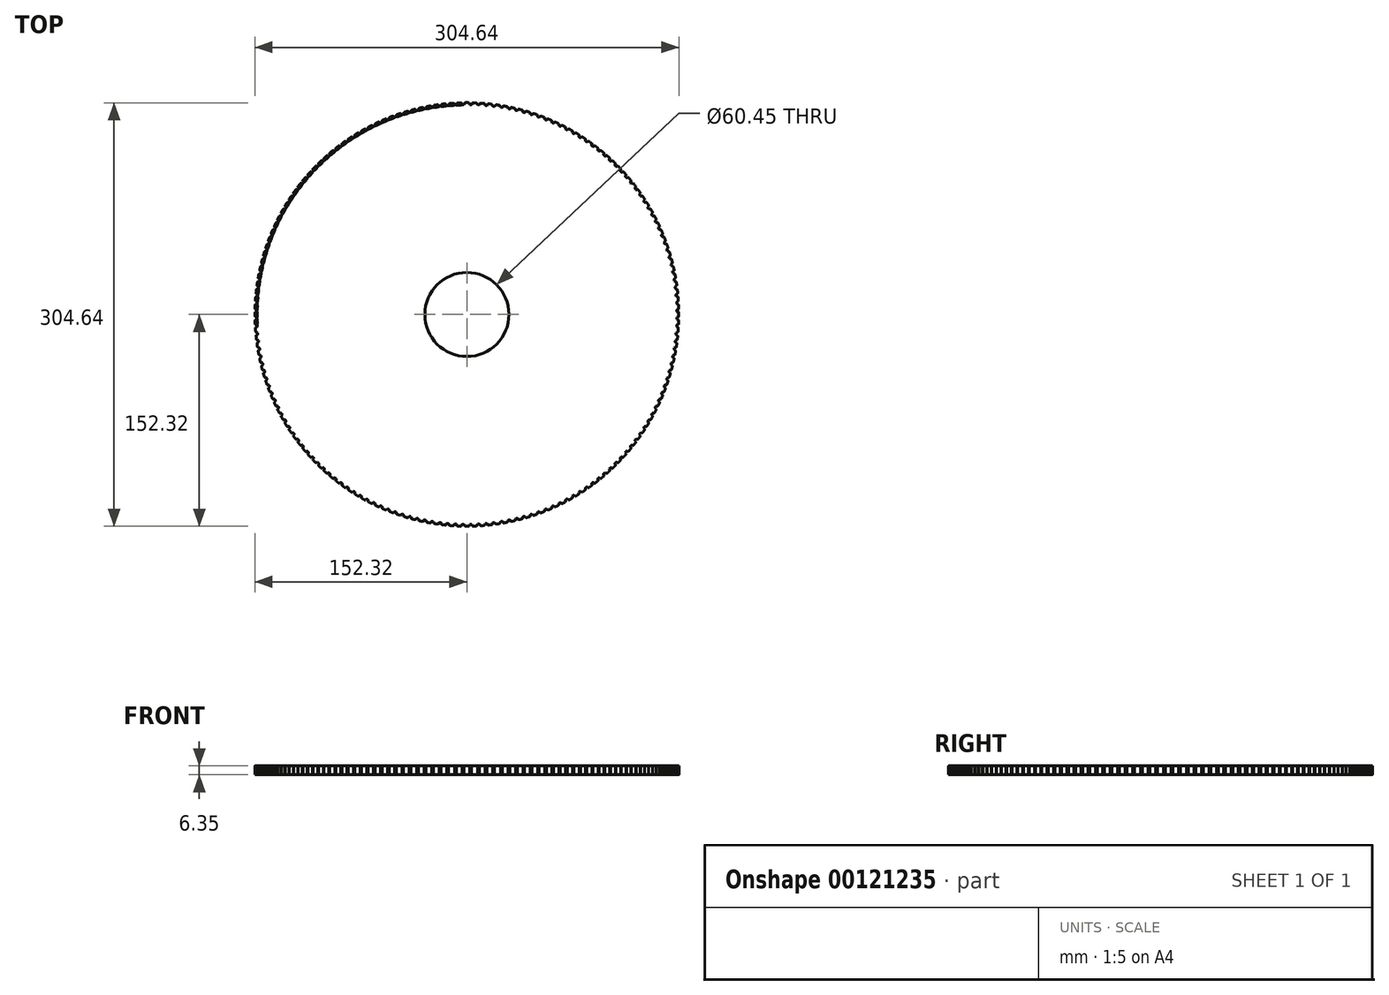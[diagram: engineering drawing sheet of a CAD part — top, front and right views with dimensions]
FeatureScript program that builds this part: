
annotation { "Feature Type Name" : "Feature", "Feature Type Description" : "" }
export const myFeature = defineFeature(function(context is Context, id is Id, definition is map)
    precondition{}
    {
        {
            var Q0;
            Q0=qCreatedBy(makeId("Top.planeOp"),FACE);
            var sketch = newSketch(context, id + "F0", { "sketchPlane" : qUnion([Q0])});
            skCircle(sketch, "E0", {"center": v(0, 0) * mm, "radius": 151 * mm});
            skSolve(sketch);
        }
        {
            var Q0;
            Q0=qSketchRegion(id+"F0",true);
            extrude(context, id + "F1", {"entities" : qUnion([Q0]), "depth" : 6.35 * mm});
        }
        {
            var Q0;
            Q0=qCreatedBy(makeId("Top.planeOp"),FACE);
            var sketch = newSketch(context, id + "F2", { "sketchPlane" : qUnion([Q0])});
            skLineSegment(sketch, "E1", {"start": v(0, -0.08) * mm, "end": v(0, 183.08) * mm, "construction": true});
            skArc(sketch, "E2", {"start": v(1.26, 152.32) * mm, "mid": v(0, 152.32) * mm, "end": v(-1.26, 152.32) * mm});
            skLineSegment(sketch, "E3", {"start": v(-1.6, 152.1) * mm, "end": v(-2.1, 151.02) * mm});
            skLineSegment(sketch, "E4", {"start": v(1.6, 152.1) * mm, "end": v(2.1, 151.02) * mm});
            skPoint(sketch, "E5.visualSharp", {"position": v(-1.5, 152.32) * mm});
            skArc(sketch, "E5.filletArc", {"start": v(-1.26, 152.32) * mm, "mid": v(-1.46, 152.26) * mm, "end": v(-1.6, 152.1) * mm});
            skPoint(sketch, "E6.visualSharp", {"position": v(1.5, 152.32) * mm});
            skArc(sketch, "E6.filletArc", {"start": v(1.6, 152.1) * mm, "mid": v(1.46, 152.26) * mm, "end": v(1.26, 152.32) * mm});
            skArc(sketch, "E7", {"start": v(-2.27, 150.9) * mm, "mid": v(-2.17, 150.94) * mm, "end": v(-2.1, 151.02) * mm});
            skArc(sketch, "E8", {"start": v(2.1, 151.02) * mm, "mid": v(2.17, 150.94) * mm, "end": v(2.27, 150.9) * mm});
            skPoint(sketch, "E9.orphan", {"position": v(2.15, 150.91) * mm});
            skArc(sketch, "E10", {"start": v(-2.27, 150.9) * mm, "mid": v(0, 150.67) * mm, "end": v(2.27, 150.9) * mm});
            skSolve(sketch);
        }
        {
            var Q0;
            Q0=makeQuery(id+"F2.imprint","IMPRINT",FACE,{"disambiguationData":[TD([[makeQuery(id+"F2.imprint","IMPRINT",EDGE,{"derivedFrom":sQuery(id+"F2.wireOp",EDGE,"E2")}),1.0]])]});
            var Q1;
            Q1=makeQuery(id+"F2.imprint","IMPRINT",FACE,{"disambiguationData":[TD([[makeQuery(id+"F2.imprint","IMPRINT",EDGE,{"derivedFrom":sQuery(id+"F2.wireOp",EDGE,"bbfa1fc5-6552-4957-9194-8f10230bb92c.0")}),1.0]])]});
            var Q2;
            Q2=makeQuery(id+"F1.opExtrude","CAP_FACE",FACE,{"disambiguationData":[OSD([sQuery(id+"F0.wireOp",EDGE,"E0")])],"isStart":false});
            extrude(context, id + "F3", {"entities" : qUnion([Q0, Q1]), "endBound" : BoundingType.UP_TO_SURFACE, "endBoundEntityFace" : qUnion([Q2]), "depth" : 25.4 * mm});
        }
        {
            var Q0;
            Q0=qCreatedBy(makeId("Front.planeOp"),FACE);
            var sketch = newSketch(context, id + "F4", { "sketchPlane" : qUnion([Q0])});
            skLineSegment(sketch, "E11", {"start": v(0, 74.48) * mm, "end": v(0, -67.78) * mm, "construction": true});
            skSolve(sketch);
        }
        {
            var Q0;
            Q0=makeQuery(id+"F3.opExtrude","SWEPT_BODY",BODY,{"disambiguationData":[OSD([sQuery(id+"F2.wireOp",EDGE,"E2"),sQuery(id+"F2.wireOp",EDGE,"E3"),sQuery(id+"F2.wireOp",EDGE,"E4"),sQuery(id+"F2.wireOp",EDGE,"E5.filletArc"),sQuery(id+"F2.wireOp",EDGE,"E6.filletArc"),sQuery(id+"F2.wireOp",EDGE,"E7"),sQuery(id+"F2.wireOp",EDGE,"E8"),sQuery(id+"F2.wireOp",EDGE,"E10")])]});
            var Q1;
            Q1=sQuery(id+"F4.wireOp",EDGE,"E11");
            circularPattern(context, id + "F5", {"entities" : qUnion([Q0]), "axis" : qUnion([Q1]), "angle" : 360 * degree, "instanceCount" : 172, "equalSpace" : true});
        }
        {
            var Q0;
            Q0=makeQuery(id+"F1.opExtrude","SWEPT_BODY",BODY,{"disambiguationData":[OSD([sQuery(id+"F0.wireOp",EDGE,"E0")])]});
            var Q1;
            Q1=makeQuery(id+"F3.opExtrude","SWEPT_BODY",BODY,{"disambiguationData":[OSD([sQuery(id+"F2.wireOp",EDGE,"E2"),sQuery(id+"F2.wireOp",EDGE,"E3"),sQuery(id+"F2.wireOp",EDGE,"E4"),sQuery(id+"F2.wireOp",EDGE,"E5.filletArc"),sQuery(id+"F2.wireOp",EDGE,"E6.filletArc"),sQuery(id+"F2.wireOp",EDGE,"E7"),sQuery(id+"F2.wireOp",EDGE,"E8"),sQuery(id+"F2.wireOp",EDGE,"E10")])]});
            var Q2;
            Q2=makeQuery(id+"F5.opPattern","COPY",BODY,{"derivedFrom":makeQuery(id+"F3.opExtrude","SWEPT_BODY",BODY,{"disambiguationData":[OSD([sQuery(id+"F2.wireOp",EDGE,"E2"),sQuery(id+"F2.wireOp",EDGE,"E3"),sQuery(id+"F2.wireOp",EDGE,"E4"),sQuery(id+"F2.wireOp",EDGE,"E5.filletArc"),sQuery(id+"F2.wireOp",EDGE,"E6.filletArc"),sQuery(id+"F2.wireOp",EDGE,"E7"),sQuery(id+"F2.wireOp",EDGE,"E8"),sQuery(id+"F2.wireOp",EDGE,"E10")])]}),"instanceName":"1"});
            var Q3;
            Q3=makeQuery(id+"F5.opPattern","COPY",BODY,{"derivedFrom":makeQuery(id+"F3.opExtrude","SWEPT_BODY",BODY,{"disambiguationData":[OSD([sQuery(id+"F2.wireOp",EDGE,"E2"),sQuery(id+"F2.wireOp",EDGE,"E3"),sQuery(id+"F2.wireOp",EDGE,"E4"),sQuery(id+"F2.wireOp",EDGE,"E5.filletArc"),sQuery(id+"F2.wireOp",EDGE,"E6.filletArc"),sQuery(id+"F2.wireOp",EDGE,"E7"),sQuery(id+"F2.wireOp",EDGE,"E8"),sQuery(id+"F2.wireOp",EDGE,"E10")])]}),"instanceName":"2"});
            var Q4;
            Q4=makeQuery(id+"F5.opPattern","COPY",BODY,{"derivedFrom":makeQuery(id+"F3.opExtrude","SWEPT_BODY",BODY,{"disambiguationData":[OSD([sQuery(id+"F2.wireOp",EDGE,"E2"),sQuery(id+"F2.wireOp",EDGE,"E3"),sQuery(id+"F2.wireOp",EDGE,"E4"),sQuery(id+"F2.wireOp",EDGE,"E5.filletArc"),sQuery(id+"F2.wireOp",EDGE,"E6.filletArc"),sQuery(id+"F2.wireOp",EDGE,"E7"),sQuery(id+"F2.wireOp",EDGE,"E8"),sQuery(id+"F2.wireOp",EDGE,"E10")])]}),"instanceName":"3"});
            var Q5;
            Q5=makeQuery(id+"F5.opPattern","COPY",BODY,{"derivedFrom":makeQuery(id+"F3.opExtrude","SWEPT_BODY",BODY,{"disambiguationData":[OSD([sQuery(id+"F2.wireOp",EDGE,"E2"),sQuery(id+"F2.wireOp",EDGE,"E3"),sQuery(id+"F2.wireOp",EDGE,"E4"),sQuery(id+"F2.wireOp",EDGE,"E5.filletArc"),sQuery(id+"F2.wireOp",EDGE,"E6.filletArc"),sQuery(id+"F2.wireOp",EDGE,"E7"),sQuery(id+"F2.wireOp",EDGE,"E8"),sQuery(id+"F2.wireOp",EDGE,"E10")])]}),"instanceName":"4"});
            var Q6;
            Q6=makeQuery(id+"F5.opPattern","COPY",BODY,{"derivedFrom":makeQuery(id+"F3.opExtrude","SWEPT_BODY",BODY,{"disambiguationData":[OSD([sQuery(id+"F2.wireOp",EDGE,"E2"),sQuery(id+"F2.wireOp",EDGE,"E3"),sQuery(id+"F2.wireOp",EDGE,"E4"),sQuery(id+"F2.wireOp",EDGE,"E5.filletArc"),sQuery(id+"F2.wireOp",EDGE,"E6.filletArc"),sQuery(id+"F2.wireOp",EDGE,"E7"),sQuery(id+"F2.wireOp",EDGE,"E8"),sQuery(id+"F2.wireOp",EDGE,"E10")])]}),"instanceName":"5"});
            var Q7;
            Q7=makeQuery(id+"F5.opPattern","COPY",BODY,{"derivedFrom":makeQuery(id+"F3.opExtrude","SWEPT_BODY",BODY,{"disambiguationData":[OSD([sQuery(id+"F2.wireOp",EDGE,"E2"),sQuery(id+"F2.wireOp",EDGE,"E3"),sQuery(id+"F2.wireOp",EDGE,"E4"),sQuery(id+"F2.wireOp",EDGE,"E5.filletArc"),sQuery(id+"F2.wireOp",EDGE,"E6.filletArc"),sQuery(id+"F2.wireOp",EDGE,"E7"),sQuery(id+"F2.wireOp",EDGE,"E8"),sQuery(id+"F2.wireOp",EDGE,"E10")])]}),"instanceName":"6"});
            var Q8;
            Q8=makeQuery(id+"F5.opPattern","COPY",BODY,{"derivedFrom":makeQuery(id+"F3.opExtrude","SWEPT_BODY",BODY,{"disambiguationData":[OSD([sQuery(id+"F2.wireOp",EDGE,"E2"),sQuery(id+"F2.wireOp",EDGE,"E3"),sQuery(id+"F2.wireOp",EDGE,"E4"),sQuery(id+"F2.wireOp",EDGE,"E5.filletArc"),sQuery(id+"F2.wireOp",EDGE,"E6.filletArc"),sQuery(id+"F2.wireOp",EDGE,"E7"),sQuery(id+"F2.wireOp",EDGE,"E8"),sQuery(id+"F2.wireOp",EDGE,"E10")])]}),"instanceName":"7"});
            var Q9;
            Q9=makeQuery(id+"F5.opPattern","COPY",BODY,{"derivedFrom":makeQuery(id+"F3.opExtrude","SWEPT_BODY",BODY,{"disambiguationData":[OSD([sQuery(id+"F2.wireOp",EDGE,"E2"),sQuery(id+"F2.wireOp",EDGE,"E3"),sQuery(id+"F2.wireOp",EDGE,"E4"),sQuery(id+"F2.wireOp",EDGE,"E5.filletArc"),sQuery(id+"F2.wireOp",EDGE,"E6.filletArc"),sQuery(id+"F2.wireOp",EDGE,"E7"),sQuery(id+"F2.wireOp",EDGE,"E8"),sQuery(id+"F2.wireOp",EDGE,"E10")])]}),"instanceName":"8"});
            var Q10;
            Q10=makeQuery(id+"F5.opPattern","COPY",BODY,{"derivedFrom":makeQuery(id+"F3.opExtrude","SWEPT_BODY",BODY,{"disambiguationData":[OSD([sQuery(id+"F2.wireOp",EDGE,"E2"),sQuery(id+"F2.wireOp",EDGE,"E3"),sQuery(id+"F2.wireOp",EDGE,"E4"),sQuery(id+"F2.wireOp",EDGE,"E5.filletArc"),sQuery(id+"F2.wireOp",EDGE,"E6.filletArc"),sQuery(id+"F2.wireOp",EDGE,"E7"),sQuery(id+"F2.wireOp",EDGE,"E8"),sQuery(id+"F2.wireOp",EDGE,"E10")])]}),"instanceName":"9"});
            var Q11;
            Q11=makeQuery(id+"F5.opPattern","COPY",BODY,{"derivedFrom":makeQuery(id+"F3.opExtrude","SWEPT_BODY",BODY,{"disambiguationData":[OSD([sQuery(id+"F2.wireOp",EDGE,"E2"),sQuery(id+"F2.wireOp",EDGE,"E3"),sQuery(id+"F2.wireOp",EDGE,"E4"),sQuery(id+"F2.wireOp",EDGE,"E5.filletArc"),sQuery(id+"F2.wireOp",EDGE,"E6.filletArc"),sQuery(id+"F2.wireOp",EDGE,"E7"),sQuery(id+"F2.wireOp",EDGE,"E8"),sQuery(id+"F2.wireOp",EDGE,"E10")])]}),"instanceName":"10"});
            var Q12;
            Q12=makeQuery(id+"F5.opPattern","COPY",BODY,{"derivedFrom":makeQuery(id+"F3.opExtrude","SWEPT_BODY",BODY,{"disambiguationData":[OSD([sQuery(id+"F2.wireOp",EDGE,"E2"),sQuery(id+"F2.wireOp",EDGE,"E3"),sQuery(id+"F2.wireOp",EDGE,"E4"),sQuery(id+"F2.wireOp",EDGE,"E5.filletArc"),sQuery(id+"F2.wireOp",EDGE,"E6.filletArc"),sQuery(id+"F2.wireOp",EDGE,"E7"),sQuery(id+"F2.wireOp",EDGE,"E8"),sQuery(id+"F2.wireOp",EDGE,"E10")])]}),"instanceName":"11"});
            var Q13;
            Q13=makeQuery(id+"F5.opPattern","COPY",BODY,{"derivedFrom":makeQuery(id+"F3.opExtrude","SWEPT_BODY",BODY,{"disambiguationData":[OSD([sQuery(id+"F2.wireOp",EDGE,"E2"),sQuery(id+"F2.wireOp",EDGE,"E3"),sQuery(id+"F2.wireOp",EDGE,"E4"),sQuery(id+"F2.wireOp",EDGE,"E5.filletArc"),sQuery(id+"F2.wireOp",EDGE,"E6.filletArc"),sQuery(id+"F2.wireOp",EDGE,"E7"),sQuery(id+"F2.wireOp",EDGE,"E8"),sQuery(id+"F2.wireOp",EDGE,"E10")])]}),"instanceName":"12"});
            var Q14;
            Q14=makeQuery(id+"F5.opPattern","COPY",BODY,{"derivedFrom":makeQuery(id+"F3.opExtrude","SWEPT_BODY",BODY,{"disambiguationData":[OSD([sQuery(id+"F2.wireOp",EDGE,"E2"),sQuery(id+"F2.wireOp",EDGE,"E3"),sQuery(id+"F2.wireOp",EDGE,"E4"),sQuery(id+"F2.wireOp",EDGE,"E5.filletArc"),sQuery(id+"F2.wireOp",EDGE,"E6.filletArc"),sQuery(id+"F2.wireOp",EDGE,"E7"),sQuery(id+"F2.wireOp",EDGE,"E8"),sQuery(id+"F2.wireOp",EDGE,"E10")])]}),"instanceName":"13"});
            var Q15;
            Q15=makeQuery(id+"F5.opPattern","COPY",BODY,{"derivedFrom":makeQuery(id+"F3.opExtrude","SWEPT_BODY",BODY,{"disambiguationData":[OSD([sQuery(id+"F2.wireOp",EDGE,"E2"),sQuery(id+"F2.wireOp",EDGE,"E3"),sQuery(id+"F2.wireOp",EDGE,"E4"),sQuery(id+"F2.wireOp",EDGE,"E5.filletArc"),sQuery(id+"F2.wireOp",EDGE,"E6.filletArc"),sQuery(id+"F2.wireOp",EDGE,"E7"),sQuery(id+"F2.wireOp",EDGE,"E8"),sQuery(id+"F2.wireOp",EDGE,"E10")])]}),"instanceName":"14"});
            var Q16;
            Q16=makeQuery(id+"F5.opPattern","COPY",BODY,{"derivedFrom":makeQuery(id+"F3.opExtrude","SWEPT_BODY",BODY,{"disambiguationData":[OSD([sQuery(id+"F2.wireOp",EDGE,"E2"),sQuery(id+"F2.wireOp",EDGE,"E3"),sQuery(id+"F2.wireOp",EDGE,"E4"),sQuery(id+"F2.wireOp",EDGE,"E5.filletArc"),sQuery(id+"F2.wireOp",EDGE,"E6.filletArc"),sQuery(id+"F2.wireOp",EDGE,"E7"),sQuery(id+"F2.wireOp",EDGE,"E8"),sQuery(id+"F2.wireOp",EDGE,"E10")])]}),"instanceName":"15"});
            var Q17;
            Q17=makeQuery(id+"F5.opPattern","COPY",BODY,{"derivedFrom":makeQuery(id+"F3.opExtrude","SWEPT_BODY",BODY,{"disambiguationData":[OSD([sQuery(id+"F2.wireOp",EDGE,"E2"),sQuery(id+"F2.wireOp",EDGE,"E3"),sQuery(id+"F2.wireOp",EDGE,"E4"),sQuery(id+"F2.wireOp",EDGE,"E5.filletArc"),sQuery(id+"F2.wireOp",EDGE,"E6.filletArc"),sQuery(id+"F2.wireOp",EDGE,"E7"),sQuery(id+"F2.wireOp",EDGE,"E8"),sQuery(id+"F2.wireOp",EDGE,"E10")])]}),"instanceName":"16"});
            var Q18;
            Q18=makeQuery(id+"F5.opPattern","COPY",BODY,{"derivedFrom":makeQuery(id+"F3.opExtrude","SWEPT_BODY",BODY,{"disambiguationData":[OSD([sQuery(id+"F2.wireOp",EDGE,"E2"),sQuery(id+"F2.wireOp",EDGE,"E3"),sQuery(id+"F2.wireOp",EDGE,"E4"),sQuery(id+"F2.wireOp",EDGE,"E5.filletArc"),sQuery(id+"F2.wireOp",EDGE,"E6.filletArc"),sQuery(id+"F2.wireOp",EDGE,"E7"),sQuery(id+"F2.wireOp",EDGE,"E8"),sQuery(id+"F2.wireOp",EDGE,"E10")])]}),"instanceName":"17"});
            var Q19;
            Q19=makeQuery(id+"F5.opPattern","COPY",BODY,{"derivedFrom":makeQuery(id+"F3.opExtrude","SWEPT_BODY",BODY,{"disambiguationData":[OSD([sQuery(id+"F2.wireOp",EDGE,"E2"),sQuery(id+"F2.wireOp",EDGE,"E3"),sQuery(id+"F2.wireOp",EDGE,"E4"),sQuery(id+"F2.wireOp",EDGE,"E5.filletArc"),sQuery(id+"F2.wireOp",EDGE,"E6.filletArc"),sQuery(id+"F2.wireOp",EDGE,"E7"),sQuery(id+"F2.wireOp",EDGE,"E8"),sQuery(id+"F2.wireOp",EDGE,"E10")])]}),"instanceName":"18"});
            var Q20;
            Q20=makeQuery(id+"F5.opPattern","COPY",BODY,{"derivedFrom":makeQuery(id+"F3.opExtrude","SWEPT_BODY",BODY,{"disambiguationData":[OSD([sQuery(id+"F2.wireOp",EDGE,"E2"),sQuery(id+"F2.wireOp",EDGE,"E3"),sQuery(id+"F2.wireOp",EDGE,"E4"),sQuery(id+"F2.wireOp",EDGE,"E5.filletArc"),sQuery(id+"F2.wireOp",EDGE,"E6.filletArc"),sQuery(id+"F2.wireOp",EDGE,"E7"),sQuery(id+"F2.wireOp",EDGE,"E8"),sQuery(id+"F2.wireOp",EDGE,"E10")])]}),"instanceName":"19"});
            var Q21;
            Q21=makeQuery(id+"F5.opPattern","COPY",BODY,{"derivedFrom":makeQuery(id+"F3.opExtrude","SWEPT_BODY",BODY,{"disambiguationData":[OSD([sQuery(id+"F2.wireOp",EDGE,"E2"),sQuery(id+"F2.wireOp",EDGE,"E3"),sQuery(id+"F2.wireOp",EDGE,"E4"),sQuery(id+"F2.wireOp",EDGE,"E5.filletArc"),sQuery(id+"F2.wireOp",EDGE,"E6.filletArc"),sQuery(id+"F2.wireOp",EDGE,"E7"),sQuery(id+"F2.wireOp",EDGE,"E8"),sQuery(id+"F2.wireOp",EDGE,"E10")])]}),"instanceName":"20"});
            var Q22;
            Q22=makeQuery(id+"F5.opPattern","COPY",BODY,{"derivedFrom":makeQuery(id+"F3.opExtrude","SWEPT_BODY",BODY,{"disambiguationData":[OSD([sQuery(id+"F2.wireOp",EDGE,"E2"),sQuery(id+"F2.wireOp",EDGE,"E3"),sQuery(id+"F2.wireOp",EDGE,"E4"),sQuery(id+"F2.wireOp",EDGE,"E5.filletArc"),sQuery(id+"F2.wireOp",EDGE,"E6.filletArc"),sQuery(id+"F2.wireOp",EDGE,"E7"),sQuery(id+"F2.wireOp",EDGE,"E8"),sQuery(id+"F2.wireOp",EDGE,"E10")])]}),"instanceName":"21"});
            var Q23;
            Q23=makeQuery(id+"F5.opPattern","COPY",BODY,{"derivedFrom":makeQuery(id+"F3.opExtrude","SWEPT_BODY",BODY,{"disambiguationData":[OSD([sQuery(id+"F2.wireOp",EDGE,"E2"),sQuery(id+"F2.wireOp",EDGE,"E3"),sQuery(id+"F2.wireOp",EDGE,"E4"),sQuery(id+"F2.wireOp",EDGE,"E5.filletArc"),sQuery(id+"F2.wireOp",EDGE,"E6.filletArc"),sQuery(id+"F2.wireOp",EDGE,"E7"),sQuery(id+"F2.wireOp",EDGE,"E8"),sQuery(id+"F2.wireOp",EDGE,"E10")])]}),"instanceName":"22"});
            var Q24;
            Q24=makeQuery(id+"F5.opPattern","COPY",BODY,{"derivedFrom":makeQuery(id+"F3.opExtrude","SWEPT_BODY",BODY,{"disambiguationData":[OSD([sQuery(id+"F2.wireOp",EDGE,"E2"),sQuery(id+"F2.wireOp",EDGE,"E3"),sQuery(id+"F2.wireOp",EDGE,"E4"),sQuery(id+"F2.wireOp",EDGE,"E5.filletArc"),sQuery(id+"F2.wireOp",EDGE,"E6.filletArc"),sQuery(id+"F2.wireOp",EDGE,"E7"),sQuery(id+"F2.wireOp",EDGE,"E8"),sQuery(id+"F2.wireOp",EDGE,"E10")])]}),"instanceName":"23"});
            var Q25;
            Q25=makeQuery(id+"F5.opPattern","COPY",BODY,{"derivedFrom":makeQuery(id+"F3.opExtrude","SWEPT_BODY",BODY,{"disambiguationData":[OSD([sQuery(id+"F2.wireOp",EDGE,"E2"),sQuery(id+"F2.wireOp",EDGE,"E3"),sQuery(id+"F2.wireOp",EDGE,"E4"),sQuery(id+"F2.wireOp",EDGE,"E5.filletArc"),sQuery(id+"F2.wireOp",EDGE,"E6.filletArc"),sQuery(id+"F2.wireOp",EDGE,"E7"),sQuery(id+"F2.wireOp",EDGE,"E8"),sQuery(id+"F2.wireOp",EDGE,"E10")])]}),"instanceName":"24"});
            var Q26;
            Q26=makeQuery(id+"F5.opPattern","COPY",BODY,{"derivedFrom":makeQuery(id+"F3.opExtrude","SWEPT_BODY",BODY,{"disambiguationData":[OSD([sQuery(id+"F2.wireOp",EDGE,"E2"),sQuery(id+"F2.wireOp",EDGE,"E3"),sQuery(id+"F2.wireOp",EDGE,"E4"),sQuery(id+"F2.wireOp",EDGE,"E5.filletArc"),sQuery(id+"F2.wireOp",EDGE,"E6.filletArc"),sQuery(id+"F2.wireOp",EDGE,"E7"),sQuery(id+"F2.wireOp",EDGE,"E8"),sQuery(id+"F2.wireOp",EDGE,"E10")])]}),"instanceName":"25"});
            var Q27;
            Q27=makeQuery(id+"F5.opPattern","COPY",BODY,{"derivedFrom":makeQuery(id+"F3.opExtrude","SWEPT_BODY",BODY,{"disambiguationData":[OSD([sQuery(id+"F2.wireOp",EDGE,"E2"),sQuery(id+"F2.wireOp",EDGE,"E3"),sQuery(id+"F2.wireOp",EDGE,"E4"),sQuery(id+"F2.wireOp",EDGE,"E5.filletArc"),sQuery(id+"F2.wireOp",EDGE,"E6.filletArc"),sQuery(id+"F2.wireOp",EDGE,"E7"),sQuery(id+"F2.wireOp",EDGE,"E8"),sQuery(id+"F2.wireOp",EDGE,"E10")])]}),"instanceName":"26"});
            var Q28;
            Q28=makeQuery(id+"F5.opPattern","COPY",BODY,{"derivedFrom":makeQuery(id+"F3.opExtrude","SWEPT_BODY",BODY,{"disambiguationData":[OSD([sQuery(id+"F2.wireOp",EDGE,"E2"),sQuery(id+"F2.wireOp",EDGE,"E3"),sQuery(id+"F2.wireOp",EDGE,"E4"),sQuery(id+"F2.wireOp",EDGE,"E5.filletArc"),sQuery(id+"F2.wireOp",EDGE,"E6.filletArc"),sQuery(id+"F2.wireOp",EDGE,"E7"),sQuery(id+"F2.wireOp",EDGE,"E8"),sQuery(id+"F2.wireOp",EDGE,"E10")])]}),"instanceName":"27"});
            var Q29;
            Q29=makeQuery(id+"F5.opPattern","COPY",BODY,{"derivedFrom":makeQuery(id+"F3.opExtrude","SWEPT_BODY",BODY,{"disambiguationData":[OSD([sQuery(id+"F2.wireOp",EDGE,"E2"),sQuery(id+"F2.wireOp",EDGE,"E3"),sQuery(id+"F2.wireOp",EDGE,"E4"),sQuery(id+"F2.wireOp",EDGE,"E5.filletArc"),sQuery(id+"F2.wireOp",EDGE,"E6.filletArc"),sQuery(id+"F2.wireOp",EDGE,"E7"),sQuery(id+"F2.wireOp",EDGE,"E8"),sQuery(id+"F2.wireOp",EDGE,"E10")])]}),"instanceName":"28"});
            var Q30;
            Q30=makeQuery(id+"F5.opPattern","COPY",BODY,{"derivedFrom":makeQuery(id+"F3.opExtrude","SWEPT_BODY",BODY,{"disambiguationData":[OSD([sQuery(id+"F2.wireOp",EDGE,"E2"),sQuery(id+"F2.wireOp",EDGE,"E3"),sQuery(id+"F2.wireOp",EDGE,"E4"),sQuery(id+"F2.wireOp",EDGE,"E5.filletArc"),sQuery(id+"F2.wireOp",EDGE,"E6.filletArc"),sQuery(id+"F2.wireOp",EDGE,"E7"),sQuery(id+"F2.wireOp",EDGE,"E8"),sQuery(id+"F2.wireOp",EDGE,"E10")])]}),"instanceName":"29"});
            var Q31;
            Q31=makeQuery(id+"F5.opPattern","COPY",BODY,{"derivedFrom":makeQuery(id+"F3.opExtrude","SWEPT_BODY",BODY,{"disambiguationData":[OSD([sQuery(id+"F2.wireOp",EDGE,"E2"),sQuery(id+"F2.wireOp",EDGE,"E3"),sQuery(id+"F2.wireOp",EDGE,"E4"),sQuery(id+"F2.wireOp",EDGE,"E5.filletArc"),sQuery(id+"F2.wireOp",EDGE,"E6.filletArc"),sQuery(id+"F2.wireOp",EDGE,"E7"),sQuery(id+"F2.wireOp",EDGE,"E8"),sQuery(id+"F2.wireOp",EDGE,"E10")])]}),"instanceName":"30"});
            var Q32;
            Q32=makeQuery(id+"F5.opPattern","COPY",BODY,{"derivedFrom":makeQuery(id+"F3.opExtrude","SWEPT_BODY",BODY,{"disambiguationData":[OSD([sQuery(id+"F2.wireOp",EDGE,"E2"),sQuery(id+"F2.wireOp",EDGE,"E3"),sQuery(id+"F2.wireOp",EDGE,"E4"),sQuery(id+"F2.wireOp",EDGE,"E5.filletArc"),sQuery(id+"F2.wireOp",EDGE,"E6.filletArc"),sQuery(id+"F2.wireOp",EDGE,"E7"),sQuery(id+"F2.wireOp",EDGE,"E8"),sQuery(id+"F2.wireOp",EDGE,"E10")])]}),"instanceName":"31"});
            var Q33;
            Q33=makeQuery(id+"F5.opPattern","COPY",BODY,{"derivedFrom":makeQuery(id+"F3.opExtrude","SWEPT_BODY",BODY,{"disambiguationData":[OSD([sQuery(id+"F2.wireOp",EDGE,"E2"),sQuery(id+"F2.wireOp",EDGE,"E3"),sQuery(id+"F2.wireOp",EDGE,"E4"),sQuery(id+"F2.wireOp",EDGE,"E5.filletArc"),sQuery(id+"F2.wireOp",EDGE,"E6.filletArc"),sQuery(id+"F2.wireOp",EDGE,"E7"),sQuery(id+"F2.wireOp",EDGE,"E8"),sQuery(id+"F2.wireOp",EDGE,"E10")])]}),"instanceName":"32"});
            var Q34;
            Q34=makeQuery(id+"F5.opPattern","COPY",BODY,{"derivedFrom":makeQuery(id+"F3.opExtrude","SWEPT_BODY",BODY,{"disambiguationData":[OSD([sQuery(id+"F2.wireOp",EDGE,"E2"),sQuery(id+"F2.wireOp",EDGE,"E3"),sQuery(id+"F2.wireOp",EDGE,"E4"),sQuery(id+"F2.wireOp",EDGE,"E5.filletArc"),sQuery(id+"F2.wireOp",EDGE,"E6.filletArc"),sQuery(id+"F2.wireOp",EDGE,"E7"),sQuery(id+"F2.wireOp",EDGE,"E8"),sQuery(id+"F2.wireOp",EDGE,"E10")])]}),"instanceName":"33"});
            var Q35;
            Q35=makeQuery(id+"F5.opPattern","COPY",BODY,{"derivedFrom":makeQuery(id+"F3.opExtrude","SWEPT_BODY",BODY,{"disambiguationData":[OSD([sQuery(id+"F2.wireOp",EDGE,"E2"),sQuery(id+"F2.wireOp",EDGE,"E3"),sQuery(id+"F2.wireOp",EDGE,"E4"),sQuery(id+"F2.wireOp",EDGE,"E5.filletArc"),sQuery(id+"F2.wireOp",EDGE,"E6.filletArc"),sQuery(id+"F2.wireOp",EDGE,"E7"),sQuery(id+"F2.wireOp",EDGE,"E8"),sQuery(id+"F2.wireOp",EDGE,"E10")])]}),"instanceName":"34"});
            var Q36;
            Q36=makeQuery(id+"F5.opPattern","COPY",BODY,{"derivedFrom":makeQuery(id+"F3.opExtrude","SWEPT_BODY",BODY,{"disambiguationData":[OSD([sQuery(id+"F2.wireOp",EDGE,"E2"),sQuery(id+"F2.wireOp",EDGE,"E3"),sQuery(id+"F2.wireOp",EDGE,"E4"),sQuery(id+"F2.wireOp",EDGE,"E5.filletArc"),sQuery(id+"F2.wireOp",EDGE,"E6.filletArc"),sQuery(id+"F2.wireOp",EDGE,"E7"),sQuery(id+"F2.wireOp",EDGE,"E8"),sQuery(id+"F2.wireOp",EDGE,"E10")])]}),"instanceName":"35"});
            var Q37;
            Q37=makeQuery(id+"F5.opPattern","COPY",BODY,{"derivedFrom":makeQuery(id+"F3.opExtrude","SWEPT_BODY",BODY,{"disambiguationData":[OSD([sQuery(id+"F2.wireOp",EDGE,"E2"),sQuery(id+"F2.wireOp",EDGE,"E3"),sQuery(id+"F2.wireOp",EDGE,"E4"),sQuery(id+"F2.wireOp",EDGE,"E5.filletArc"),sQuery(id+"F2.wireOp",EDGE,"E6.filletArc"),sQuery(id+"F2.wireOp",EDGE,"E7"),sQuery(id+"F2.wireOp",EDGE,"E8"),sQuery(id+"F2.wireOp",EDGE,"E10")])]}),"instanceName":"36"});
            var Q38;
            Q38=makeQuery(id+"F5.opPattern","COPY",BODY,{"derivedFrom":makeQuery(id+"F3.opExtrude","SWEPT_BODY",BODY,{"disambiguationData":[OSD([sQuery(id+"F2.wireOp",EDGE,"E2"),sQuery(id+"F2.wireOp",EDGE,"E3"),sQuery(id+"F2.wireOp",EDGE,"E4"),sQuery(id+"F2.wireOp",EDGE,"E5.filletArc"),sQuery(id+"F2.wireOp",EDGE,"E6.filletArc"),sQuery(id+"F2.wireOp",EDGE,"E7"),sQuery(id+"F2.wireOp",EDGE,"E8"),sQuery(id+"F2.wireOp",EDGE,"E10")])]}),"instanceName":"37"});
            var Q39;
            Q39=makeQuery(id+"F5.opPattern","COPY",BODY,{"derivedFrom":makeQuery(id+"F3.opExtrude","SWEPT_BODY",BODY,{"disambiguationData":[OSD([sQuery(id+"F2.wireOp",EDGE,"E2"),sQuery(id+"F2.wireOp",EDGE,"E3"),sQuery(id+"F2.wireOp",EDGE,"E4"),sQuery(id+"F2.wireOp",EDGE,"E5.filletArc"),sQuery(id+"F2.wireOp",EDGE,"E6.filletArc"),sQuery(id+"F2.wireOp",EDGE,"E7"),sQuery(id+"F2.wireOp",EDGE,"E8"),sQuery(id+"F2.wireOp",EDGE,"E10")])]}),"instanceName":"38"});
            var Q40;
            Q40=makeQuery(id+"F5.opPattern","COPY",BODY,{"derivedFrom":makeQuery(id+"F3.opExtrude","SWEPT_BODY",BODY,{"disambiguationData":[OSD([sQuery(id+"F2.wireOp",EDGE,"E2"),sQuery(id+"F2.wireOp",EDGE,"E3"),sQuery(id+"F2.wireOp",EDGE,"E4"),sQuery(id+"F2.wireOp",EDGE,"E5.filletArc"),sQuery(id+"F2.wireOp",EDGE,"E6.filletArc"),sQuery(id+"F2.wireOp",EDGE,"E7"),sQuery(id+"F2.wireOp",EDGE,"E8"),sQuery(id+"F2.wireOp",EDGE,"E10")])]}),"instanceName":"39"});
            var Q41;
            Q41=makeQuery(id+"F5.opPattern","COPY",BODY,{"derivedFrom":makeQuery(id+"F3.opExtrude","SWEPT_BODY",BODY,{"disambiguationData":[OSD([sQuery(id+"F2.wireOp",EDGE,"E2"),sQuery(id+"F2.wireOp",EDGE,"E3"),sQuery(id+"F2.wireOp",EDGE,"E4"),sQuery(id+"F2.wireOp",EDGE,"E5.filletArc"),sQuery(id+"F2.wireOp",EDGE,"E6.filletArc"),sQuery(id+"F2.wireOp",EDGE,"E7"),sQuery(id+"F2.wireOp",EDGE,"E8"),sQuery(id+"F2.wireOp",EDGE,"E10")])]}),"instanceName":"40"});
            var Q42;
            Q42=makeQuery(id+"F5.opPattern","COPY",BODY,{"derivedFrom":makeQuery(id+"F3.opExtrude","SWEPT_BODY",BODY,{"disambiguationData":[OSD([sQuery(id+"F2.wireOp",EDGE,"E2"),sQuery(id+"F2.wireOp",EDGE,"E3"),sQuery(id+"F2.wireOp",EDGE,"E4"),sQuery(id+"F2.wireOp",EDGE,"E5.filletArc"),sQuery(id+"F2.wireOp",EDGE,"E6.filletArc"),sQuery(id+"F2.wireOp",EDGE,"E7"),sQuery(id+"F2.wireOp",EDGE,"E8"),sQuery(id+"F2.wireOp",EDGE,"E10")])]}),"instanceName":"41"});
            var Q43;
            Q43=makeQuery(id+"F5.opPattern","COPY",BODY,{"derivedFrom":makeQuery(id+"F3.opExtrude","SWEPT_BODY",BODY,{"disambiguationData":[OSD([sQuery(id+"F2.wireOp",EDGE,"E2"),sQuery(id+"F2.wireOp",EDGE,"E3"),sQuery(id+"F2.wireOp",EDGE,"E4"),sQuery(id+"F2.wireOp",EDGE,"E5.filletArc"),sQuery(id+"F2.wireOp",EDGE,"E6.filletArc"),sQuery(id+"F2.wireOp",EDGE,"E7"),sQuery(id+"F2.wireOp",EDGE,"E8"),sQuery(id+"F2.wireOp",EDGE,"E10")])]}),"instanceName":"42"});
            var Q44;
            Q44=makeQuery(id+"F5.opPattern","COPY",BODY,{"derivedFrom":makeQuery(id+"F3.opExtrude","SWEPT_BODY",BODY,{"disambiguationData":[OSD([sQuery(id+"F2.wireOp",EDGE,"E2"),sQuery(id+"F2.wireOp",EDGE,"E3"),sQuery(id+"F2.wireOp",EDGE,"E4"),sQuery(id+"F2.wireOp",EDGE,"E5.filletArc"),sQuery(id+"F2.wireOp",EDGE,"E6.filletArc"),sQuery(id+"F2.wireOp",EDGE,"E7"),sQuery(id+"F2.wireOp",EDGE,"E8"),sQuery(id+"F2.wireOp",EDGE,"E10")])]}),"instanceName":"43"});
            var Q45;
            Q45=makeQuery(id+"F5.opPattern","COPY",BODY,{"derivedFrom":makeQuery(id+"F3.opExtrude","SWEPT_BODY",BODY,{"disambiguationData":[OSD([sQuery(id+"F2.wireOp",EDGE,"E2"),sQuery(id+"F2.wireOp",EDGE,"E3"),sQuery(id+"F2.wireOp",EDGE,"E4"),sQuery(id+"F2.wireOp",EDGE,"E5.filletArc"),sQuery(id+"F2.wireOp",EDGE,"E6.filletArc"),sQuery(id+"F2.wireOp",EDGE,"E7"),sQuery(id+"F2.wireOp",EDGE,"E8"),sQuery(id+"F2.wireOp",EDGE,"E10")])]}),"instanceName":"44"});
            var Q46;
            Q46=makeQuery(id+"F5.opPattern","COPY",BODY,{"derivedFrom":makeQuery(id+"F3.opExtrude","SWEPT_BODY",BODY,{"disambiguationData":[OSD([sQuery(id+"F2.wireOp",EDGE,"E2"),sQuery(id+"F2.wireOp",EDGE,"E3"),sQuery(id+"F2.wireOp",EDGE,"E4"),sQuery(id+"F2.wireOp",EDGE,"E5.filletArc"),sQuery(id+"F2.wireOp",EDGE,"E6.filletArc"),sQuery(id+"F2.wireOp",EDGE,"E7"),sQuery(id+"F2.wireOp",EDGE,"E8"),sQuery(id+"F2.wireOp",EDGE,"E10")])]}),"instanceName":"45"});
            var Q47;
            Q47=makeQuery(id+"F5.opPattern","COPY",BODY,{"derivedFrom":makeQuery(id+"F3.opExtrude","SWEPT_BODY",BODY,{"disambiguationData":[OSD([sQuery(id+"F2.wireOp",EDGE,"E2"),sQuery(id+"F2.wireOp",EDGE,"E3"),sQuery(id+"F2.wireOp",EDGE,"E4"),sQuery(id+"F2.wireOp",EDGE,"E5.filletArc"),sQuery(id+"F2.wireOp",EDGE,"E6.filletArc"),sQuery(id+"F2.wireOp",EDGE,"E7"),sQuery(id+"F2.wireOp",EDGE,"E8"),sQuery(id+"F2.wireOp",EDGE,"E10")])]}),"instanceName":"46"});
            var Q48;
            Q48=makeQuery(id+"F5.opPattern","COPY",BODY,{"derivedFrom":makeQuery(id+"F3.opExtrude","SWEPT_BODY",BODY,{"disambiguationData":[OSD([sQuery(id+"F2.wireOp",EDGE,"E2"),sQuery(id+"F2.wireOp",EDGE,"E3"),sQuery(id+"F2.wireOp",EDGE,"E4"),sQuery(id+"F2.wireOp",EDGE,"E5.filletArc"),sQuery(id+"F2.wireOp",EDGE,"E6.filletArc"),sQuery(id+"F2.wireOp",EDGE,"E7"),sQuery(id+"F2.wireOp",EDGE,"E8"),sQuery(id+"F2.wireOp",EDGE,"E10")])]}),"instanceName":"47"});
            var Q49;
            Q49=makeQuery(id+"F5.opPattern","COPY",BODY,{"derivedFrom":makeQuery(id+"F3.opExtrude","SWEPT_BODY",BODY,{"disambiguationData":[OSD([sQuery(id+"F2.wireOp",EDGE,"E2"),sQuery(id+"F2.wireOp",EDGE,"E3"),sQuery(id+"F2.wireOp",EDGE,"E4"),sQuery(id+"F2.wireOp",EDGE,"E5.filletArc"),sQuery(id+"F2.wireOp",EDGE,"E6.filletArc"),sQuery(id+"F2.wireOp",EDGE,"E7"),sQuery(id+"F2.wireOp",EDGE,"E8"),sQuery(id+"F2.wireOp",EDGE,"E10")])]}),"instanceName":"48"});
            var Q50;
            Q50=makeQuery(id+"F5.opPattern","COPY",BODY,{"derivedFrom":makeQuery(id+"F3.opExtrude","SWEPT_BODY",BODY,{"disambiguationData":[OSD([sQuery(id+"F2.wireOp",EDGE,"E2"),sQuery(id+"F2.wireOp",EDGE,"E3"),sQuery(id+"F2.wireOp",EDGE,"E4"),sQuery(id+"F2.wireOp",EDGE,"E5.filletArc"),sQuery(id+"F2.wireOp",EDGE,"E6.filletArc"),sQuery(id+"F2.wireOp",EDGE,"E7"),sQuery(id+"F2.wireOp",EDGE,"E8"),sQuery(id+"F2.wireOp",EDGE,"E10")])]}),"instanceName":"49"});
            var Q51;
            Q51=makeQuery(id+"F5.opPattern","COPY",BODY,{"derivedFrom":makeQuery(id+"F3.opExtrude","SWEPT_BODY",BODY,{"disambiguationData":[OSD([sQuery(id+"F2.wireOp",EDGE,"E2"),sQuery(id+"F2.wireOp",EDGE,"E3"),sQuery(id+"F2.wireOp",EDGE,"E4"),sQuery(id+"F2.wireOp",EDGE,"E5.filletArc"),sQuery(id+"F2.wireOp",EDGE,"E6.filletArc"),sQuery(id+"F2.wireOp",EDGE,"E7"),sQuery(id+"F2.wireOp",EDGE,"E8"),sQuery(id+"F2.wireOp",EDGE,"E10")])]}),"instanceName":"50"});
            var Q52;
            Q52=makeQuery(id+"F5.opPattern","COPY",BODY,{"derivedFrom":makeQuery(id+"F3.opExtrude","SWEPT_BODY",BODY,{"disambiguationData":[OSD([sQuery(id+"F2.wireOp",EDGE,"E2"),sQuery(id+"F2.wireOp",EDGE,"E3"),sQuery(id+"F2.wireOp",EDGE,"E4"),sQuery(id+"F2.wireOp",EDGE,"E5.filletArc"),sQuery(id+"F2.wireOp",EDGE,"E6.filletArc"),sQuery(id+"F2.wireOp",EDGE,"E7"),sQuery(id+"F2.wireOp",EDGE,"E8"),sQuery(id+"F2.wireOp",EDGE,"E10")])]}),"instanceName":"51"});
            var Q53;
            Q53=makeQuery(id+"F5.opPattern","COPY",BODY,{"derivedFrom":makeQuery(id+"F3.opExtrude","SWEPT_BODY",BODY,{"disambiguationData":[OSD([sQuery(id+"F2.wireOp",EDGE,"E2"),sQuery(id+"F2.wireOp",EDGE,"E3"),sQuery(id+"F2.wireOp",EDGE,"E4"),sQuery(id+"F2.wireOp",EDGE,"E5.filletArc"),sQuery(id+"F2.wireOp",EDGE,"E6.filletArc"),sQuery(id+"F2.wireOp",EDGE,"E7"),sQuery(id+"F2.wireOp",EDGE,"E8"),sQuery(id+"F2.wireOp",EDGE,"E10")])]}),"instanceName":"52"});
            var Q54;
            Q54=makeQuery(id+"F5.opPattern","COPY",BODY,{"derivedFrom":makeQuery(id+"F3.opExtrude","SWEPT_BODY",BODY,{"disambiguationData":[OSD([sQuery(id+"F2.wireOp",EDGE,"E2"),sQuery(id+"F2.wireOp",EDGE,"E3"),sQuery(id+"F2.wireOp",EDGE,"E4"),sQuery(id+"F2.wireOp",EDGE,"E5.filletArc"),sQuery(id+"F2.wireOp",EDGE,"E6.filletArc"),sQuery(id+"F2.wireOp",EDGE,"E7"),sQuery(id+"F2.wireOp",EDGE,"E8"),sQuery(id+"F2.wireOp",EDGE,"E10")])]}),"instanceName":"53"});
            var Q55;
            Q55=makeQuery(id+"F5.opPattern","COPY",BODY,{"derivedFrom":makeQuery(id+"F3.opExtrude","SWEPT_BODY",BODY,{"disambiguationData":[OSD([sQuery(id+"F2.wireOp",EDGE,"E2"),sQuery(id+"F2.wireOp",EDGE,"E3"),sQuery(id+"F2.wireOp",EDGE,"E4"),sQuery(id+"F2.wireOp",EDGE,"E5.filletArc"),sQuery(id+"F2.wireOp",EDGE,"E6.filletArc"),sQuery(id+"F2.wireOp",EDGE,"E7"),sQuery(id+"F2.wireOp",EDGE,"E8"),sQuery(id+"F2.wireOp",EDGE,"E10")])]}),"instanceName":"54"});
            var Q56;
            Q56=makeQuery(id+"F5.opPattern","COPY",BODY,{"derivedFrom":makeQuery(id+"F3.opExtrude","SWEPT_BODY",BODY,{"disambiguationData":[OSD([sQuery(id+"F2.wireOp",EDGE,"E2"),sQuery(id+"F2.wireOp",EDGE,"E3"),sQuery(id+"F2.wireOp",EDGE,"E4"),sQuery(id+"F2.wireOp",EDGE,"E5.filletArc"),sQuery(id+"F2.wireOp",EDGE,"E6.filletArc"),sQuery(id+"F2.wireOp",EDGE,"E7"),sQuery(id+"F2.wireOp",EDGE,"E8"),sQuery(id+"F2.wireOp",EDGE,"E10")])]}),"instanceName":"55"});
            var Q57;
            Q57=makeQuery(id+"F5.opPattern","COPY",BODY,{"derivedFrom":makeQuery(id+"F3.opExtrude","SWEPT_BODY",BODY,{"disambiguationData":[OSD([sQuery(id+"F2.wireOp",EDGE,"E2"),sQuery(id+"F2.wireOp",EDGE,"E3"),sQuery(id+"F2.wireOp",EDGE,"E4"),sQuery(id+"F2.wireOp",EDGE,"E5.filletArc"),sQuery(id+"F2.wireOp",EDGE,"E6.filletArc"),sQuery(id+"F2.wireOp",EDGE,"E7"),sQuery(id+"F2.wireOp",EDGE,"E8"),sQuery(id+"F2.wireOp",EDGE,"E10")])]}),"instanceName":"56"});
            var Q58;
            Q58=makeQuery(id+"F5.opPattern","COPY",BODY,{"derivedFrom":makeQuery(id+"F3.opExtrude","SWEPT_BODY",BODY,{"disambiguationData":[OSD([sQuery(id+"F2.wireOp",EDGE,"E2"),sQuery(id+"F2.wireOp",EDGE,"E3"),sQuery(id+"F2.wireOp",EDGE,"E4"),sQuery(id+"F2.wireOp",EDGE,"E5.filletArc"),sQuery(id+"F2.wireOp",EDGE,"E6.filletArc"),sQuery(id+"F2.wireOp",EDGE,"E7"),sQuery(id+"F2.wireOp",EDGE,"E8"),sQuery(id+"F2.wireOp",EDGE,"E10")])]}),"instanceName":"57"});
            var Q59;
            Q59=makeQuery(id+"F5.opPattern","COPY",BODY,{"derivedFrom":makeQuery(id+"F3.opExtrude","SWEPT_BODY",BODY,{"disambiguationData":[OSD([sQuery(id+"F2.wireOp",EDGE,"E2"),sQuery(id+"F2.wireOp",EDGE,"E3"),sQuery(id+"F2.wireOp",EDGE,"E4"),sQuery(id+"F2.wireOp",EDGE,"E5.filletArc"),sQuery(id+"F2.wireOp",EDGE,"E6.filletArc"),sQuery(id+"F2.wireOp",EDGE,"E7"),sQuery(id+"F2.wireOp",EDGE,"E8"),sQuery(id+"F2.wireOp",EDGE,"E10")])]}),"instanceName":"58"});
            var Q60;
            Q60=makeQuery(id+"F5.opPattern","COPY",BODY,{"derivedFrom":makeQuery(id+"F3.opExtrude","SWEPT_BODY",BODY,{"disambiguationData":[OSD([sQuery(id+"F2.wireOp",EDGE,"E2"),sQuery(id+"F2.wireOp",EDGE,"E3"),sQuery(id+"F2.wireOp",EDGE,"E4"),sQuery(id+"F2.wireOp",EDGE,"E5.filletArc"),sQuery(id+"F2.wireOp",EDGE,"E6.filletArc"),sQuery(id+"F2.wireOp",EDGE,"E7"),sQuery(id+"F2.wireOp",EDGE,"E8"),sQuery(id+"F2.wireOp",EDGE,"E10")])]}),"instanceName":"59"});
            var Q61;
            Q61=makeQuery(id+"F5.opPattern","COPY",BODY,{"derivedFrom":makeQuery(id+"F3.opExtrude","SWEPT_BODY",BODY,{"disambiguationData":[OSD([sQuery(id+"F2.wireOp",EDGE,"E2"),sQuery(id+"F2.wireOp",EDGE,"E3"),sQuery(id+"F2.wireOp",EDGE,"E4"),sQuery(id+"F2.wireOp",EDGE,"E5.filletArc"),sQuery(id+"F2.wireOp",EDGE,"E6.filletArc"),sQuery(id+"F2.wireOp",EDGE,"E7"),sQuery(id+"F2.wireOp",EDGE,"E8"),sQuery(id+"F2.wireOp",EDGE,"E10")])]}),"instanceName":"60"});
            var Q62;
            Q62=makeQuery(id+"F5.opPattern","COPY",BODY,{"derivedFrom":makeQuery(id+"F3.opExtrude","SWEPT_BODY",BODY,{"disambiguationData":[OSD([sQuery(id+"F2.wireOp",EDGE,"E2"),sQuery(id+"F2.wireOp",EDGE,"E3"),sQuery(id+"F2.wireOp",EDGE,"E4"),sQuery(id+"F2.wireOp",EDGE,"E5.filletArc"),sQuery(id+"F2.wireOp",EDGE,"E6.filletArc"),sQuery(id+"F2.wireOp",EDGE,"E7"),sQuery(id+"F2.wireOp",EDGE,"E8"),sQuery(id+"F2.wireOp",EDGE,"E10")])]}),"instanceName":"61"});
            var Q63;
            Q63=makeQuery(id+"F5.opPattern","COPY",BODY,{"derivedFrom":makeQuery(id+"F3.opExtrude","SWEPT_BODY",BODY,{"disambiguationData":[OSD([sQuery(id+"F2.wireOp",EDGE,"E2"),sQuery(id+"F2.wireOp",EDGE,"E3"),sQuery(id+"F2.wireOp",EDGE,"E4"),sQuery(id+"F2.wireOp",EDGE,"E5.filletArc"),sQuery(id+"F2.wireOp",EDGE,"E6.filletArc"),sQuery(id+"F2.wireOp",EDGE,"E7"),sQuery(id+"F2.wireOp",EDGE,"E8"),sQuery(id+"F2.wireOp",EDGE,"E10")])]}),"instanceName":"62"});
            var Q64;
            Q64=makeQuery(id+"F5.opPattern","COPY",BODY,{"derivedFrom":makeQuery(id+"F3.opExtrude","SWEPT_BODY",BODY,{"disambiguationData":[OSD([sQuery(id+"F2.wireOp",EDGE,"E2"),sQuery(id+"F2.wireOp",EDGE,"E3"),sQuery(id+"F2.wireOp",EDGE,"E4"),sQuery(id+"F2.wireOp",EDGE,"E5.filletArc"),sQuery(id+"F2.wireOp",EDGE,"E6.filletArc"),sQuery(id+"F2.wireOp",EDGE,"E7"),sQuery(id+"F2.wireOp",EDGE,"E8"),sQuery(id+"F2.wireOp",EDGE,"E10")])]}),"instanceName":"63"});
            var Q65;
            Q65=makeQuery(id+"F5.opPattern","COPY",BODY,{"derivedFrom":makeQuery(id+"F3.opExtrude","SWEPT_BODY",BODY,{"disambiguationData":[OSD([sQuery(id+"F2.wireOp",EDGE,"E2"),sQuery(id+"F2.wireOp",EDGE,"E3"),sQuery(id+"F2.wireOp",EDGE,"E4"),sQuery(id+"F2.wireOp",EDGE,"E5.filletArc"),sQuery(id+"F2.wireOp",EDGE,"E6.filletArc"),sQuery(id+"F2.wireOp",EDGE,"E7"),sQuery(id+"F2.wireOp",EDGE,"E8"),sQuery(id+"F2.wireOp",EDGE,"E10")])]}),"instanceName":"64"});
            var Q66;
            Q66=makeQuery(id+"F5.opPattern","COPY",BODY,{"derivedFrom":makeQuery(id+"F3.opExtrude","SWEPT_BODY",BODY,{"disambiguationData":[OSD([sQuery(id+"F2.wireOp",EDGE,"E2"),sQuery(id+"F2.wireOp",EDGE,"E3"),sQuery(id+"F2.wireOp",EDGE,"E4"),sQuery(id+"F2.wireOp",EDGE,"E5.filletArc"),sQuery(id+"F2.wireOp",EDGE,"E6.filletArc"),sQuery(id+"F2.wireOp",EDGE,"E7"),sQuery(id+"F2.wireOp",EDGE,"E8"),sQuery(id+"F2.wireOp",EDGE,"E10")])]}),"instanceName":"65"});
            var Q67;
            Q67=makeQuery(id+"F5.opPattern","COPY",BODY,{"derivedFrom":makeQuery(id+"F3.opExtrude","SWEPT_BODY",BODY,{"disambiguationData":[OSD([sQuery(id+"F2.wireOp",EDGE,"E2"),sQuery(id+"F2.wireOp",EDGE,"E3"),sQuery(id+"F2.wireOp",EDGE,"E4"),sQuery(id+"F2.wireOp",EDGE,"E5.filletArc"),sQuery(id+"F2.wireOp",EDGE,"E6.filletArc"),sQuery(id+"F2.wireOp",EDGE,"E7"),sQuery(id+"F2.wireOp",EDGE,"E8"),sQuery(id+"F2.wireOp",EDGE,"E10")])]}),"instanceName":"66"});
            var Q68;
            Q68=makeQuery(id+"F5.opPattern","COPY",BODY,{"derivedFrom":makeQuery(id+"F3.opExtrude","SWEPT_BODY",BODY,{"disambiguationData":[OSD([sQuery(id+"F2.wireOp",EDGE,"E2"),sQuery(id+"F2.wireOp",EDGE,"E3"),sQuery(id+"F2.wireOp",EDGE,"E4"),sQuery(id+"F2.wireOp",EDGE,"E5.filletArc"),sQuery(id+"F2.wireOp",EDGE,"E6.filletArc"),sQuery(id+"F2.wireOp",EDGE,"E7"),sQuery(id+"F2.wireOp",EDGE,"E8"),sQuery(id+"F2.wireOp",EDGE,"E10")])]}),"instanceName":"67"});
            var Q69;
            Q69=makeQuery(id+"F5.opPattern","COPY",BODY,{"derivedFrom":makeQuery(id+"F3.opExtrude","SWEPT_BODY",BODY,{"disambiguationData":[OSD([sQuery(id+"F2.wireOp",EDGE,"E2"),sQuery(id+"F2.wireOp",EDGE,"E3"),sQuery(id+"F2.wireOp",EDGE,"E4"),sQuery(id+"F2.wireOp",EDGE,"E5.filletArc"),sQuery(id+"F2.wireOp",EDGE,"E6.filletArc"),sQuery(id+"F2.wireOp",EDGE,"E7"),sQuery(id+"F2.wireOp",EDGE,"E8"),sQuery(id+"F2.wireOp",EDGE,"E10")])]}),"instanceName":"68"});
            var Q70;
            Q70=makeQuery(id+"F5.opPattern","COPY",BODY,{"derivedFrom":makeQuery(id+"F3.opExtrude","SWEPT_BODY",BODY,{"disambiguationData":[OSD([sQuery(id+"F2.wireOp",EDGE,"E2"),sQuery(id+"F2.wireOp",EDGE,"E3"),sQuery(id+"F2.wireOp",EDGE,"E4"),sQuery(id+"F2.wireOp",EDGE,"E5.filletArc"),sQuery(id+"F2.wireOp",EDGE,"E6.filletArc"),sQuery(id+"F2.wireOp",EDGE,"E7"),sQuery(id+"F2.wireOp",EDGE,"E8"),sQuery(id+"F2.wireOp",EDGE,"E10")])]}),"instanceName":"69"});
            var Q71;
            Q71=makeQuery(id+"F5.opPattern","COPY",BODY,{"derivedFrom":makeQuery(id+"F3.opExtrude","SWEPT_BODY",BODY,{"disambiguationData":[OSD([sQuery(id+"F2.wireOp",EDGE,"E2"),sQuery(id+"F2.wireOp",EDGE,"E3"),sQuery(id+"F2.wireOp",EDGE,"E4"),sQuery(id+"F2.wireOp",EDGE,"E5.filletArc"),sQuery(id+"F2.wireOp",EDGE,"E6.filletArc"),sQuery(id+"F2.wireOp",EDGE,"E7"),sQuery(id+"F2.wireOp",EDGE,"E8"),sQuery(id+"F2.wireOp",EDGE,"E10")])]}),"instanceName":"70"});
            var Q72;
            Q72=makeQuery(id+"F5.opPattern","COPY",BODY,{"derivedFrom":makeQuery(id+"F3.opExtrude","SWEPT_BODY",BODY,{"disambiguationData":[OSD([sQuery(id+"F2.wireOp",EDGE,"E2"),sQuery(id+"F2.wireOp",EDGE,"E3"),sQuery(id+"F2.wireOp",EDGE,"E4"),sQuery(id+"F2.wireOp",EDGE,"E5.filletArc"),sQuery(id+"F2.wireOp",EDGE,"E6.filletArc"),sQuery(id+"F2.wireOp",EDGE,"E7"),sQuery(id+"F2.wireOp",EDGE,"E8"),sQuery(id+"F2.wireOp",EDGE,"E10")])]}),"instanceName":"71"});
            var Q73;
            Q73=makeQuery(id+"F5.opPattern","COPY",BODY,{"derivedFrom":makeQuery(id+"F3.opExtrude","SWEPT_BODY",BODY,{"disambiguationData":[OSD([sQuery(id+"F2.wireOp",EDGE,"E2"),sQuery(id+"F2.wireOp",EDGE,"E3"),sQuery(id+"F2.wireOp",EDGE,"E4"),sQuery(id+"F2.wireOp",EDGE,"E5.filletArc"),sQuery(id+"F2.wireOp",EDGE,"E6.filletArc"),sQuery(id+"F2.wireOp",EDGE,"E7"),sQuery(id+"F2.wireOp",EDGE,"E8"),sQuery(id+"F2.wireOp",EDGE,"E10")])]}),"instanceName":"72"});
            var Q74;
            Q74=makeQuery(id+"F5.opPattern","COPY",BODY,{"derivedFrom":makeQuery(id+"F3.opExtrude","SWEPT_BODY",BODY,{"disambiguationData":[OSD([sQuery(id+"F2.wireOp",EDGE,"E2"),sQuery(id+"F2.wireOp",EDGE,"E3"),sQuery(id+"F2.wireOp",EDGE,"E4"),sQuery(id+"F2.wireOp",EDGE,"E5.filletArc"),sQuery(id+"F2.wireOp",EDGE,"E6.filletArc"),sQuery(id+"F2.wireOp",EDGE,"E7"),sQuery(id+"F2.wireOp",EDGE,"E8"),sQuery(id+"F2.wireOp",EDGE,"E10")])]}),"instanceName":"73"});
            var Q75;
            Q75=makeQuery(id+"F5.opPattern","COPY",BODY,{"derivedFrom":makeQuery(id+"F3.opExtrude","SWEPT_BODY",BODY,{"disambiguationData":[OSD([sQuery(id+"F2.wireOp",EDGE,"E2"),sQuery(id+"F2.wireOp",EDGE,"E3"),sQuery(id+"F2.wireOp",EDGE,"E4"),sQuery(id+"F2.wireOp",EDGE,"E5.filletArc"),sQuery(id+"F2.wireOp",EDGE,"E6.filletArc"),sQuery(id+"F2.wireOp",EDGE,"E7"),sQuery(id+"F2.wireOp",EDGE,"E8"),sQuery(id+"F2.wireOp",EDGE,"E10")])]}),"instanceName":"74"});
            var Q76;
            Q76=makeQuery(id+"F5.opPattern","COPY",BODY,{"derivedFrom":makeQuery(id+"F3.opExtrude","SWEPT_BODY",BODY,{"disambiguationData":[OSD([sQuery(id+"F2.wireOp",EDGE,"E2"),sQuery(id+"F2.wireOp",EDGE,"E3"),sQuery(id+"F2.wireOp",EDGE,"E4"),sQuery(id+"F2.wireOp",EDGE,"E5.filletArc"),sQuery(id+"F2.wireOp",EDGE,"E6.filletArc"),sQuery(id+"F2.wireOp",EDGE,"E7"),sQuery(id+"F2.wireOp",EDGE,"E8"),sQuery(id+"F2.wireOp",EDGE,"E10")])]}),"instanceName":"75"});
            var Q77;
            Q77=makeQuery(id+"F5.opPattern","COPY",BODY,{"derivedFrom":makeQuery(id+"F3.opExtrude","SWEPT_BODY",BODY,{"disambiguationData":[OSD([sQuery(id+"F2.wireOp",EDGE,"E2"),sQuery(id+"F2.wireOp",EDGE,"E3"),sQuery(id+"F2.wireOp",EDGE,"E4"),sQuery(id+"F2.wireOp",EDGE,"E5.filletArc"),sQuery(id+"F2.wireOp",EDGE,"E6.filletArc"),sQuery(id+"F2.wireOp",EDGE,"E7"),sQuery(id+"F2.wireOp",EDGE,"E8"),sQuery(id+"F2.wireOp",EDGE,"E10")])]}),"instanceName":"76"});
            var Q78;
            Q78=makeQuery(id+"F5.opPattern","COPY",BODY,{"derivedFrom":makeQuery(id+"F3.opExtrude","SWEPT_BODY",BODY,{"disambiguationData":[OSD([sQuery(id+"F2.wireOp",EDGE,"E2"),sQuery(id+"F2.wireOp",EDGE,"E3"),sQuery(id+"F2.wireOp",EDGE,"E4"),sQuery(id+"F2.wireOp",EDGE,"E5.filletArc"),sQuery(id+"F2.wireOp",EDGE,"E6.filletArc"),sQuery(id+"F2.wireOp",EDGE,"E7"),sQuery(id+"F2.wireOp",EDGE,"E8"),sQuery(id+"F2.wireOp",EDGE,"E10")])]}),"instanceName":"77"});
            var Q79;
            Q79=makeQuery(id+"F5.opPattern","COPY",BODY,{"derivedFrom":makeQuery(id+"F3.opExtrude","SWEPT_BODY",BODY,{"disambiguationData":[OSD([sQuery(id+"F2.wireOp",EDGE,"E2"),sQuery(id+"F2.wireOp",EDGE,"E3"),sQuery(id+"F2.wireOp",EDGE,"E4"),sQuery(id+"F2.wireOp",EDGE,"E5.filletArc"),sQuery(id+"F2.wireOp",EDGE,"E6.filletArc"),sQuery(id+"F2.wireOp",EDGE,"E7"),sQuery(id+"F2.wireOp",EDGE,"E8"),sQuery(id+"F2.wireOp",EDGE,"E10")])]}),"instanceName":"78"});
            var Q80;
            Q80=makeQuery(id+"F5.opPattern","COPY",BODY,{"derivedFrom":makeQuery(id+"F3.opExtrude","SWEPT_BODY",BODY,{"disambiguationData":[OSD([sQuery(id+"F2.wireOp",EDGE,"E2"),sQuery(id+"F2.wireOp",EDGE,"E3"),sQuery(id+"F2.wireOp",EDGE,"E4"),sQuery(id+"F2.wireOp",EDGE,"E5.filletArc"),sQuery(id+"F2.wireOp",EDGE,"E6.filletArc"),sQuery(id+"F2.wireOp",EDGE,"E7"),sQuery(id+"F2.wireOp",EDGE,"E8"),sQuery(id+"F2.wireOp",EDGE,"E10")])]}),"instanceName":"79"});
            var Q81;
            Q81=makeQuery(id+"F5.opPattern","COPY",BODY,{"derivedFrom":makeQuery(id+"F3.opExtrude","SWEPT_BODY",BODY,{"disambiguationData":[OSD([sQuery(id+"F2.wireOp",EDGE,"E2"),sQuery(id+"F2.wireOp",EDGE,"E3"),sQuery(id+"F2.wireOp",EDGE,"E4"),sQuery(id+"F2.wireOp",EDGE,"E5.filletArc"),sQuery(id+"F2.wireOp",EDGE,"E6.filletArc"),sQuery(id+"F2.wireOp",EDGE,"E7"),sQuery(id+"F2.wireOp",EDGE,"E8"),sQuery(id+"F2.wireOp",EDGE,"E10")])]}),"instanceName":"80"});
            var Q82;
            Q82=makeQuery(id+"F5.opPattern","COPY",BODY,{"derivedFrom":makeQuery(id+"F3.opExtrude","SWEPT_BODY",BODY,{"disambiguationData":[OSD([sQuery(id+"F2.wireOp",EDGE,"E2"),sQuery(id+"F2.wireOp",EDGE,"E3"),sQuery(id+"F2.wireOp",EDGE,"E4"),sQuery(id+"F2.wireOp",EDGE,"E5.filletArc"),sQuery(id+"F2.wireOp",EDGE,"E6.filletArc"),sQuery(id+"F2.wireOp",EDGE,"E7"),sQuery(id+"F2.wireOp",EDGE,"E8"),sQuery(id+"F2.wireOp",EDGE,"E10")])]}),"instanceName":"81"});
            var Q83;
            Q83=makeQuery(id+"F5.opPattern","COPY",BODY,{"derivedFrom":makeQuery(id+"F3.opExtrude","SWEPT_BODY",BODY,{"disambiguationData":[OSD([sQuery(id+"F2.wireOp",EDGE,"E2"),sQuery(id+"F2.wireOp",EDGE,"E3"),sQuery(id+"F2.wireOp",EDGE,"E4"),sQuery(id+"F2.wireOp",EDGE,"E5.filletArc"),sQuery(id+"F2.wireOp",EDGE,"E6.filletArc"),sQuery(id+"F2.wireOp",EDGE,"E7"),sQuery(id+"F2.wireOp",EDGE,"E8"),sQuery(id+"F2.wireOp",EDGE,"E10")])]}),"instanceName":"82"});
            var Q84;
            Q84=makeQuery(id+"F5.opPattern","COPY",BODY,{"derivedFrom":makeQuery(id+"F3.opExtrude","SWEPT_BODY",BODY,{"disambiguationData":[OSD([sQuery(id+"F2.wireOp",EDGE,"E2"),sQuery(id+"F2.wireOp",EDGE,"E3"),sQuery(id+"F2.wireOp",EDGE,"E4"),sQuery(id+"F2.wireOp",EDGE,"E5.filletArc"),sQuery(id+"F2.wireOp",EDGE,"E6.filletArc"),sQuery(id+"F2.wireOp",EDGE,"E7"),sQuery(id+"F2.wireOp",EDGE,"E8"),sQuery(id+"F2.wireOp",EDGE,"E10")])]}),"instanceName":"83"});
            var Q85;
            Q85=makeQuery(id+"F5.opPattern","COPY",BODY,{"derivedFrom":makeQuery(id+"F3.opExtrude","SWEPT_BODY",BODY,{"disambiguationData":[OSD([sQuery(id+"F2.wireOp",EDGE,"E2"),sQuery(id+"F2.wireOp",EDGE,"E3"),sQuery(id+"F2.wireOp",EDGE,"E4"),sQuery(id+"F2.wireOp",EDGE,"E5.filletArc"),sQuery(id+"F2.wireOp",EDGE,"E6.filletArc"),sQuery(id+"F2.wireOp",EDGE,"E7"),sQuery(id+"F2.wireOp",EDGE,"E8"),sQuery(id+"F2.wireOp",EDGE,"E10")])]}),"instanceName":"84"});
            var Q86;
            Q86=makeQuery(id+"F5.opPattern","COPY",BODY,{"derivedFrom":makeQuery(id+"F3.opExtrude","SWEPT_BODY",BODY,{"disambiguationData":[OSD([sQuery(id+"F2.wireOp",EDGE,"E2"),sQuery(id+"F2.wireOp",EDGE,"E3"),sQuery(id+"F2.wireOp",EDGE,"E4"),sQuery(id+"F2.wireOp",EDGE,"E5.filletArc"),sQuery(id+"F2.wireOp",EDGE,"E6.filletArc"),sQuery(id+"F2.wireOp",EDGE,"E7"),sQuery(id+"F2.wireOp",EDGE,"E8"),sQuery(id+"F2.wireOp",EDGE,"E10")])]}),"instanceName":"85"});
            var Q87;
            Q87=makeQuery(id+"F5.opPattern","COPY",BODY,{"derivedFrom":makeQuery(id+"F3.opExtrude","SWEPT_BODY",BODY,{"disambiguationData":[OSD([sQuery(id+"F2.wireOp",EDGE,"E2"),sQuery(id+"F2.wireOp",EDGE,"E3"),sQuery(id+"F2.wireOp",EDGE,"E4"),sQuery(id+"F2.wireOp",EDGE,"E5.filletArc"),sQuery(id+"F2.wireOp",EDGE,"E6.filletArc"),sQuery(id+"F2.wireOp",EDGE,"E7"),sQuery(id+"F2.wireOp",EDGE,"E8"),sQuery(id+"F2.wireOp",EDGE,"E10")])]}),"instanceName":"86"});
            var Q88;
            Q88=makeQuery(id+"F5.opPattern","COPY",BODY,{"derivedFrom":makeQuery(id+"F3.opExtrude","SWEPT_BODY",BODY,{"disambiguationData":[OSD([sQuery(id+"F2.wireOp",EDGE,"E2"),sQuery(id+"F2.wireOp",EDGE,"E3"),sQuery(id+"F2.wireOp",EDGE,"E4"),sQuery(id+"F2.wireOp",EDGE,"E5.filletArc"),sQuery(id+"F2.wireOp",EDGE,"E6.filletArc"),sQuery(id+"F2.wireOp",EDGE,"E7"),sQuery(id+"F2.wireOp",EDGE,"E8"),sQuery(id+"F2.wireOp",EDGE,"E10")])]}),"instanceName":"87"});
            var Q89;
            Q89=makeQuery(id+"F5.opPattern","COPY",BODY,{"derivedFrom":makeQuery(id+"F3.opExtrude","SWEPT_BODY",BODY,{"disambiguationData":[OSD([sQuery(id+"F2.wireOp",EDGE,"E2"),sQuery(id+"F2.wireOp",EDGE,"E3"),sQuery(id+"F2.wireOp",EDGE,"E4"),sQuery(id+"F2.wireOp",EDGE,"E5.filletArc"),sQuery(id+"F2.wireOp",EDGE,"E6.filletArc"),sQuery(id+"F2.wireOp",EDGE,"E7"),sQuery(id+"F2.wireOp",EDGE,"E8"),sQuery(id+"F2.wireOp",EDGE,"E10")])]}),"instanceName":"88"});
            var Q90;
            Q90=makeQuery(id+"F5.opPattern","COPY",BODY,{"derivedFrom":makeQuery(id+"F3.opExtrude","SWEPT_BODY",BODY,{"disambiguationData":[OSD([sQuery(id+"F2.wireOp",EDGE,"E2"),sQuery(id+"F2.wireOp",EDGE,"E3"),sQuery(id+"F2.wireOp",EDGE,"E4"),sQuery(id+"F2.wireOp",EDGE,"E5.filletArc"),sQuery(id+"F2.wireOp",EDGE,"E6.filletArc"),sQuery(id+"F2.wireOp",EDGE,"E7"),sQuery(id+"F2.wireOp",EDGE,"E8"),sQuery(id+"F2.wireOp",EDGE,"E10")])]}),"instanceName":"89"});
            var Q91;
            Q91=makeQuery(id+"F5.opPattern","COPY",BODY,{"derivedFrom":makeQuery(id+"F3.opExtrude","SWEPT_BODY",BODY,{"disambiguationData":[OSD([sQuery(id+"F2.wireOp",EDGE,"E2"),sQuery(id+"F2.wireOp",EDGE,"E3"),sQuery(id+"F2.wireOp",EDGE,"E4"),sQuery(id+"F2.wireOp",EDGE,"E5.filletArc"),sQuery(id+"F2.wireOp",EDGE,"E6.filletArc"),sQuery(id+"F2.wireOp",EDGE,"E7"),sQuery(id+"F2.wireOp",EDGE,"E8"),sQuery(id+"F2.wireOp",EDGE,"E10")])]}),"instanceName":"90"});
            var Q92;
            Q92=makeQuery(id+"F5.opPattern","COPY",BODY,{"derivedFrom":makeQuery(id+"F3.opExtrude","SWEPT_BODY",BODY,{"disambiguationData":[OSD([sQuery(id+"F2.wireOp",EDGE,"E2"),sQuery(id+"F2.wireOp",EDGE,"E3"),sQuery(id+"F2.wireOp",EDGE,"E4"),sQuery(id+"F2.wireOp",EDGE,"E5.filletArc"),sQuery(id+"F2.wireOp",EDGE,"E6.filletArc"),sQuery(id+"F2.wireOp",EDGE,"E7"),sQuery(id+"F2.wireOp",EDGE,"E8"),sQuery(id+"F2.wireOp",EDGE,"E10")])]}),"instanceName":"91"});
            var Q93;
            Q93=makeQuery(id+"F5.opPattern","COPY",BODY,{"derivedFrom":makeQuery(id+"F3.opExtrude","SWEPT_BODY",BODY,{"disambiguationData":[OSD([sQuery(id+"F2.wireOp",EDGE,"E2"),sQuery(id+"F2.wireOp",EDGE,"E3"),sQuery(id+"F2.wireOp",EDGE,"E4"),sQuery(id+"F2.wireOp",EDGE,"E5.filletArc"),sQuery(id+"F2.wireOp",EDGE,"E6.filletArc"),sQuery(id+"F2.wireOp",EDGE,"E7"),sQuery(id+"F2.wireOp",EDGE,"E8"),sQuery(id+"F2.wireOp",EDGE,"E10")])]}),"instanceName":"92"});
            var Q94;
            Q94=makeQuery(id+"F5.opPattern","COPY",BODY,{"derivedFrom":makeQuery(id+"F3.opExtrude","SWEPT_BODY",BODY,{"disambiguationData":[OSD([sQuery(id+"F2.wireOp",EDGE,"E2"),sQuery(id+"F2.wireOp",EDGE,"E3"),sQuery(id+"F2.wireOp",EDGE,"E4"),sQuery(id+"F2.wireOp",EDGE,"E5.filletArc"),sQuery(id+"F2.wireOp",EDGE,"E6.filletArc"),sQuery(id+"F2.wireOp",EDGE,"E7"),sQuery(id+"F2.wireOp",EDGE,"E8"),sQuery(id+"F2.wireOp",EDGE,"E10")])]}),"instanceName":"93"});
            var Q95;
            Q95=makeQuery(id+"F5.opPattern","COPY",BODY,{"derivedFrom":makeQuery(id+"F3.opExtrude","SWEPT_BODY",BODY,{"disambiguationData":[OSD([sQuery(id+"F2.wireOp",EDGE,"E2"),sQuery(id+"F2.wireOp",EDGE,"E3"),sQuery(id+"F2.wireOp",EDGE,"E4"),sQuery(id+"F2.wireOp",EDGE,"E5.filletArc"),sQuery(id+"F2.wireOp",EDGE,"E6.filletArc"),sQuery(id+"F2.wireOp",EDGE,"E7"),sQuery(id+"F2.wireOp",EDGE,"E8"),sQuery(id+"F2.wireOp",EDGE,"E10")])]}),"instanceName":"94"});
            var Q96;
            Q96=makeQuery(id+"F5.opPattern","COPY",BODY,{"derivedFrom":makeQuery(id+"F3.opExtrude","SWEPT_BODY",BODY,{"disambiguationData":[OSD([sQuery(id+"F2.wireOp",EDGE,"E2"),sQuery(id+"F2.wireOp",EDGE,"E3"),sQuery(id+"F2.wireOp",EDGE,"E4"),sQuery(id+"F2.wireOp",EDGE,"E5.filletArc"),sQuery(id+"F2.wireOp",EDGE,"E6.filletArc"),sQuery(id+"F2.wireOp",EDGE,"E7"),sQuery(id+"F2.wireOp",EDGE,"E8"),sQuery(id+"F2.wireOp",EDGE,"E10")])]}),"instanceName":"95"});
            var Q97;
            Q97=makeQuery(id+"F5.opPattern","COPY",BODY,{"derivedFrom":makeQuery(id+"F3.opExtrude","SWEPT_BODY",BODY,{"disambiguationData":[OSD([sQuery(id+"F2.wireOp",EDGE,"E2"),sQuery(id+"F2.wireOp",EDGE,"E3"),sQuery(id+"F2.wireOp",EDGE,"E4"),sQuery(id+"F2.wireOp",EDGE,"E5.filletArc"),sQuery(id+"F2.wireOp",EDGE,"E6.filletArc"),sQuery(id+"F2.wireOp",EDGE,"E7"),sQuery(id+"F2.wireOp",EDGE,"E8"),sQuery(id+"F2.wireOp",EDGE,"E10")])]}),"instanceName":"96"});
            var Q98;
            Q98=makeQuery(id+"F5.opPattern","COPY",BODY,{"derivedFrom":makeQuery(id+"F3.opExtrude","SWEPT_BODY",BODY,{"disambiguationData":[OSD([sQuery(id+"F2.wireOp",EDGE,"E2"),sQuery(id+"F2.wireOp",EDGE,"E3"),sQuery(id+"F2.wireOp",EDGE,"E4"),sQuery(id+"F2.wireOp",EDGE,"E5.filletArc"),sQuery(id+"F2.wireOp",EDGE,"E6.filletArc"),sQuery(id+"F2.wireOp",EDGE,"E7"),sQuery(id+"F2.wireOp",EDGE,"E8"),sQuery(id+"F2.wireOp",EDGE,"E10")])]}),"instanceName":"97"});
            var Q99;
            Q99=makeQuery(id+"F5.opPattern","COPY",BODY,{"derivedFrom":makeQuery(id+"F3.opExtrude","SWEPT_BODY",BODY,{"disambiguationData":[OSD([sQuery(id+"F2.wireOp",EDGE,"E2"),sQuery(id+"F2.wireOp",EDGE,"E3"),sQuery(id+"F2.wireOp",EDGE,"E4"),sQuery(id+"F2.wireOp",EDGE,"E5.filletArc"),sQuery(id+"F2.wireOp",EDGE,"E6.filletArc"),sQuery(id+"F2.wireOp",EDGE,"E7"),sQuery(id+"F2.wireOp",EDGE,"E8"),sQuery(id+"F2.wireOp",EDGE,"E10")])]}),"instanceName":"98"});
            var Q100;
            Q100=makeQuery(id+"F5.opPattern","COPY",BODY,{"derivedFrom":makeQuery(id+"F3.opExtrude","SWEPT_BODY",BODY,{"disambiguationData":[OSD([sQuery(id+"F2.wireOp",EDGE,"E2"),sQuery(id+"F2.wireOp",EDGE,"E3"),sQuery(id+"F2.wireOp",EDGE,"E4"),sQuery(id+"F2.wireOp",EDGE,"E5.filletArc"),sQuery(id+"F2.wireOp",EDGE,"E6.filletArc"),sQuery(id+"F2.wireOp",EDGE,"E7"),sQuery(id+"F2.wireOp",EDGE,"E8"),sQuery(id+"F2.wireOp",EDGE,"E10")])]}),"instanceName":"99"});
            var Q101;
            Q101=makeQuery(id+"F5.opPattern","COPY",BODY,{"derivedFrom":makeQuery(id+"F3.opExtrude","SWEPT_BODY",BODY,{"disambiguationData":[OSD([sQuery(id+"F2.wireOp",EDGE,"E2"),sQuery(id+"F2.wireOp",EDGE,"E3"),sQuery(id+"F2.wireOp",EDGE,"E4"),sQuery(id+"F2.wireOp",EDGE,"E5.filletArc"),sQuery(id+"F2.wireOp",EDGE,"E6.filletArc"),sQuery(id+"F2.wireOp",EDGE,"E7"),sQuery(id+"F2.wireOp",EDGE,"E8"),sQuery(id+"F2.wireOp",EDGE,"E10")])]}),"instanceName":"100"});
            var Q102;
            Q102=makeQuery(id+"F5.opPattern","COPY",BODY,{"derivedFrom":makeQuery(id+"F3.opExtrude","SWEPT_BODY",BODY,{"disambiguationData":[OSD([sQuery(id+"F2.wireOp",EDGE,"E2"),sQuery(id+"F2.wireOp",EDGE,"E3"),sQuery(id+"F2.wireOp",EDGE,"E4"),sQuery(id+"F2.wireOp",EDGE,"E5.filletArc"),sQuery(id+"F2.wireOp",EDGE,"E6.filletArc"),sQuery(id+"F2.wireOp",EDGE,"E7"),sQuery(id+"F2.wireOp",EDGE,"E8"),sQuery(id+"F2.wireOp",EDGE,"E10")])]}),"instanceName":"101"});
            var Q103;
            Q103=makeQuery(id+"F5.opPattern","COPY",BODY,{"derivedFrom":makeQuery(id+"F3.opExtrude","SWEPT_BODY",BODY,{"disambiguationData":[OSD([sQuery(id+"F2.wireOp",EDGE,"E2"),sQuery(id+"F2.wireOp",EDGE,"E3"),sQuery(id+"F2.wireOp",EDGE,"E4"),sQuery(id+"F2.wireOp",EDGE,"E5.filletArc"),sQuery(id+"F2.wireOp",EDGE,"E6.filletArc"),sQuery(id+"F2.wireOp",EDGE,"E7"),sQuery(id+"F2.wireOp",EDGE,"E8"),sQuery(id+"F2.wireOp",EDGE,"E10")])]}),"instanceName":"102"});
            var Q104;
            Q104=makeQuery(id+"F5.opPattern","COPY",BODY,{"derivedFrom":makeQuery(id+"F3.opExtrude","SWEPT_BODY",BODY,{"disambiguationData":[OSD([sQuery(id+"F2.wireOp",EDGE,"E2"),sQuery(id+"F2.wireOp",EDGE,"E3"),sQuery(id+"F2.wireOp",EDGE,"E4"),sQuery(id+"F2.wireOp",EDGE,"E5.filletArc"),sQuery(id+"F2.wireOp",EDGE,"E6.filletArc"),sQuery(id+"F2.wireOp",EDGE,"E7"),sQuery(id+"F2.wireOp",EDGE,"E8"),sQuery(id+"F2.wireOp",EDGE,"E10")])]}),"instanceName":"103"});
            var Q105;
            Q105=makeQuery(id+"F5.opPattern","COPY",BODY,{"derivedFrom":makeQuery(id+"F3.opExtrude","SWEPT_BODY",BODY,{"disambiguationData":[OSD([sQuery(id+"F2.wireOp",EDGE,"E2"),sQuery(id+"F2.wireOp",EDGE,"E3"),sQuery(id+"F2.wireOp",EDGE,"E4"),sQuery(id+"F2.wireOp",EDGE,"E5.filletArc"),sQuery(id+"F2.wireOp",EDGE,"E6.filletArc"),sQuery(id+"F2.wireOp",EDGE,"E7"),sQuery(id+"F2.wireOp",EDGE,"E8"),sQuery(id+"F2.wireOp",EDGE,"E10")])]}),"instanceName":"104"});
            var Q106;
            Q106=makeQuery(id+"F5.opPattern","COPY",BODY,{"derivedFrom":makeQuery(id+"F3.opExtrude","SWEPT_BODY",BODY,{"disambiguationData":[OSD([sQuery(id+"F2.wireOp",EDGE,"E2"),sQuery(id+"F2.wireOp",EDGE,"E3"),sQuery(id+"F2.wireOp",EDGE,"E4"),sQuery(id+"F2.wireOp",EDGE,"E5.filletArc"),sQuery(id+"F2.wireOp",EDGE,"E6.filletArc"),sQuery(id+"F2.wireOp",EDGE,"E7"),sQuery(id+"F2.wireOp",EDGE,"E8"),sQuery(id+"F2.wireOp",EDGE,"E10")])]}),"instanceName":"105"});
            var Q107;
            Q107=makeQuery(id+"F5.opPattern","COPY",BODY,{"derivedFrom":makeQuery(id+"F3.opExtrude","SWEPT_BODY",BODY,{"disambiguationData":[OSD([sQuery(id+"F2.wireOp",EDGE,"E2"),sQuery(id+"F2.wireOp",EDGE,"E3"),sQuery(id+"F2.wireOp",EDGE,"E4"),sQuery(id+"F2.wireOp",EDGE,"E5.filletArc"),sQuery(id+"F2.wireOp",EDGE,"E6.filletArc"),sQuery(id+"F2.wireOp",EDGE,"E7"),sQuery(id+"F2.wireOp",EDGE,"E8"),sQuery(id+"F2.wireOp",EDGE,"E10")])]}),"instanceName":"106"});
            var Q108;
            Q108=makeQuery(id+"F5.opPattern","COPY",BODY,{"derivedFrom":makeQuery(id+"F3.opExtrude","SWEPT_BODY",BODY,{"disambiguationData":[OSD([sQuery(id+"F2.wireOp",EDGE,"E2"),sQuery(id+"F2.wireOp",EDGE,"E3"),sQuery(id+"F2.wireOp",EDGE,"E4"),sQuery(id+"F2.wireOp",EDGE,"E5.filletArc"),sQuery(id+"F2.wireOp",EDGE,"E6.filletArc"),sQuery(id+"F2.wireOp",EDGE,"E7"),sQuery(id+"F2.wireOp",EDGE,"E8"),sQuery(id+"F2.wireOp",EDGE,"E10")])]}),"instanceName":"107"});
            var Q109;
            Q109=makeQuery(id+"F5.opPattern","COPY",BODY,{"derivedFrom":makeQuery(id+"F3.opExtrude","SWEPT_BODY",BODY,{"disambiguationData":[OSD([sQuery(id+"F2.wireOp",EDGE,"E2"),sQuery(id+"F2.wireOp",EDGE,"E3"),sQuery(id+"F2.wireOp",EDGE,"E4"),sQuery(id+"F2.wireOp",EDGE,"E5.filletArc"),sQuery(id+"F2.wireOp",EDGE,"E6.filletArc"),sQuery(id+"F2.wireOp",EDGE,"E7"),sQuery(id+"F2.wireOp",EDGE,"E8"),sQuery(id+"F2.wireOp",EDGE,"E10")])]}),"instanceName":"108"});
            var Q110;
            Q110=makeQuery(id+"F5.opPattern","COPY",BODY,{"derivedFrom":makeQuery(id+"F3.opExtrude","SWEPT_BODY",BODY,{"disambiguationData":[OSD([sQuery(id+"F2.wireOp",EDGE,"E2"),sQuery(id+"F2.wireOp",EDGE,"E3"),sQuery(id+"F2.wireOp",EDGE,"E4"),sQuery(id+"F2.wireOp",EDGE,"E5.filletArc"),sQuery(id+"F2.wireOp",EDGE,"E6.filletArc"),sQuery(id+"F2.wireOp",EDGE,"E7"),sQuery(id+"F2.wireOp",EDGE,"E8"),sQuery(id+"F2.wireOp",EDGE,"E10")])]}),"instanceName":"109"});
            var Q111;
            Q111=makeQuery(id+"F5.opPattern","COPY",BODY,{"derivedFrom":makeQuery(id+"F3.opExtrude","SWEPT_BODY",BODY,{"disambiguationData":[OSD([sQuery(id+"F2.wireOp",EDGE,"E2"),sQuery(id+"F2.wireOp",EDGE,"E3"),sQuery(id+"F2.wireOp",EDGE,"E4"),sQuery(id+"F2.wireOp",EDGE,"E5.filletArc"),sQuery(id+"F2.wireOp",EDGE,"E6.filletArc"),sQuery(id+"F2.wireOp",EDGE,"E7"),sQuery(id+"F2.wireOp",EDGE,"E8"),sQuery(id+"F2.wireOp",EDGE,"E10")])]}),"instanceName":"110"});
            var Q112;
            Q112=makeQuery(id+"F5.opPattern","COPY",BODY,{"derivedFrom":makeQuery(id+"F3.opExtrude","SWEPT_BODY",BODY,{"disambiguationData":[OSD([sQuery(id+"F2.wireOp",EDGE,"E2"),sQuery(id+"F2.wireOp",EDGE,"E3"),sQuery(id+"F2.wireOp",EDGE,"E4"),sQuery(id+"F2.wireOp",EDGE,"E5.filletArc"),sQuery(id+"F2.wireOp",EDGE,"E6.filletArc"),sQuery(id+"F2.wireOp",EDGE,"E7"),sQuery(id+"F2.wireOp",EDGE,"E8"),sQuery(id+"F2.wireOp",EDGE,"E10")])]}),"instanceName":"111"});
            var Q113;
            Q113=makeQuery(id+"F5.opPattern","COPY",BODY,{"derivedFrom":makeQuery(id+"F3.opExtrude","SWEPT_BODY",BODY,{"disambiguationData":[OSD([sQuery(id+"F2.wireOp",EDGE,"E2"),sQuery(id+"F2.wireOp",EDGE,"E3"),sQuery(id+"F2.wireOp",EDGE,"E4"),sQuery(id+"F2.wireOp",EDGE,"E5.filletArc"),sQuery(id+"F2.wireOp",EDGE,"E6.filletArc"),sQuery(id+"F2.wireOp",EDGE,"E7"),sQuery(id+"F2.wireOp",EDGE,"E8"),sQuery(id+"F2.wireOp",EDGE,"E10")])]}),"instanceName":"112"});
            var Q114;
            Q114=makeQuery(id+"F5.opPattern","COPY",BODY,{"derivedFrom":makeQuery(id+"F3.opExtrude","SWEPT_BODY",BODY,{"disambiguationData":[OSD([sQuery(id+"F2.wireOp",EDGE,"E2"),sQuery(id+"F2.wireOp",EDGE,"E3"),sQuery(id+"F2.wireOp",EDGE,"E4"),sQuery(id+"F2.wireOp",EDGE,"E5.filletArc"),sQuery(id+"F2.wireOp",EDGE,"E6.filletArc"),sQuery(id+"F2.wireOp",EDGE,"E7"),sQuery(id+"F2.wireOp",EDGE,"E8"),sQuery(id+"F2.wireOp",EDGE,"E10")])]}),"instanceName":"113"});
            var Q115;
            Q115=makeQuery(id+"F5.opPattern","COPY",BODY,{"derivedFrom":makeQuery(id+"F3.opExtrude","SWEPT_BODY",BODY,{"disambiguationData":[OSD([sQuery(id+"F2.wireOp",EDGE,"E2"),sQuery(id+"F2.wireOp",EDGE,"E3"),sQuery(id+"F2.wireOp",EDGE,"E4"),sQuery(id+"F2.wireOp",EDGE,"E5.filletArc"),sQuery(id+"F2.wireOp",EDGE,"E6.filletArc"),sQuery(id+"F2.wireOp",EDGE,"E7"),sQuery(id+"F2.wireOp",EDGE,"E8"),sQuery(id+"F2.wireOp",EDGE,"E10")])]}),"instanceName":"114"});
            var Q116;
            Q116=makeQuery(id+"F5.opPattern","COPY",BODY,{"derivedFrom":makeQuery(id+"F3.opExtrude","SWEPT_BODY",BODY,{"disambiguationData":[OSD([sQuery(id+"F2.wireOp",EDGE,"E2"),sQuery(id+"F2.wireOp",EDGE,"E3"),sQuery(id+"F2.wireOp",EDGE,"E4"),sQuery(id+"F2.wireOp",EDGE,"E5.filletArc"),sQuery(id+"F2.wireOp",EDGE,"E6.filletArc"),sQuery(id+"F2.wireOp",EDGE,"E7"),sQuery(id+"F2.wireOp",EDGE,"E8"),sQuery(id+"F2.wireOp",EDGE,"E10")])]}),"instanceName":"115"});
            var Q117;
            Q117=makeQuery(id+"F5.opPattern","COPY",BODY,{"derivedFrom":makeQuery(id+"F3.opExtrude","SWEPT_BODY",BODY,{"disambiguationData":[OSD([sQuery(id+"F2.wireOp",EDGE,"E2"),sQuery(id+"F2.wireOp",EDGE,"E3"),sQuery(id+"F2.wireOp",EDGE,"E4"),sQuery(id+"F2.wireOp",EDGE,"E5.filletArc"),sQuery(id+"F2.wireOp",EDGE,"E6.filletArc"),sQuery(id+"F2.wireOp",EDGE,"E7"),sQuery(id+"F2.wireOp",EDGE,"E8"),sQuery(id+"F2.wireOp",EDGE,"E10")])]}),"instanceName":"116"});
            var Q118;
            Q118=makeQuery(id+"F5.opPattern","COPY",BODY,{"derivedFrom":makeQuery(id+"F3.opExtrude","SWEPT_BODY",BODY,{"disambiguationData":[OSD([sQuery(id+"F2.wireOp",EDGE,"E2"),sQuery(id+"F2.wireOp",EDGE,"E3"),sQuery(id+"F2.wireOp",EDGE,"E4"),sQuery(id+"F2.wireOp",EDGE,"E5.filletArc"),sQuery(id+"F2.wireOp",EDGE,"E6.filletArc"),sQuery(id+"F2.wireOp",EDGE,"E7"),sQuery(id+"F2.wireOp",EDGE,"E8"),sQuery(id+"F2.wireOp",EDGE,"E10")])]}),"instanceName":"117"});
            var Q119;
            Q119=makeQuery(id+"F5.opPattern","COPY",BODY,{"derivedFrom":makeQuery(id+"F3.opExtrude","SWEPT_BODY",BODY,{"disambiguationData":[OSD([sQuery(id+"F2.wireOp",EDGE,"E2"),sQuery(id+"F2.wireOp",EDGE,"E3"),sQuery(id+"F2.wireOp",EDGE,"E4"),sQuery(id+"F2.wireOp",EDGE,"E5.filletArc"),sQuery(id+"F2.wireOp",EDGE,"E6.filletArc"),sQuery(id+"F2.wireOp",EDGE,"E7"),sQuery(id+"F2.wireOp",EDGE,"E8"),sQuery(id+"F2.wireOp",EDGE,"E10")])]}),"instanceName":"118"});
            var Q120;
            Q120=makeQuery(id+"F5.opPattern","COPY",BODY,{"derivedFrom":makeQuery(id+"F3.opExtrude","SWEPT_BODY",BODY,{"disambiguationData":[OSD([sQuery(id+"F2.wireOp",EDGE,"E2"),sQuery(id+"F2.wireOp",EDGE,"E3"),sQuery(id+"F2.wireOp",EDGE,"E4"),sQuery(id+"F2.wireOp",EDGE,"E5.filletArc"),sQuery(id+"F2.wireOp",EDGE,"E6.filletArc"),sQuery(id+"F2.wireOp",EDGE,"E7"),sQuery(id+"F2.wireOp",EDGE,"E8"),sQuery(id+"F2.wireOp",EDGE,"E10")])]}),"instanceName":"119"});
            var Q121;
            Q121=makeQuery(id+"F5.opPattern","COPY",BODY,{"derivedFrom":makeQuery(id+"F3.opExtrude","SWEPT_BODY",BODY,{"disambiguationData":[OSD([sQuery(id+"F2.wireOp",EDGE,"E2"),sQuery(id+"F2.wireOp",EDGE,"E3"),sQuery(id+"F2.wireOp",EDGE,"E4"),sQuery(id+"F2.wireOp",EDGE,"E5.filletArc"),sQuery(id+"F2.wireOp",EDGE,"E6.filletArc"),sQuery(id+"F2.wireOp",EDGE,"E7"),sQuery(id+"F2.wireOp",EDGE,"E8"),sQuery(id+"F2.wireOp",EDGE,"E10")])]}),"instanceName":"120"});
            var Q122;
            Q122=makeQuery(id+"F5.opPattern","COPY",BODY,{"derivedFrom":makeQuery(id+"F3.opExtrude","SWEPT_BODY",BODY,{"disambiguationData":[OSD([sQuery(id+"F2.wireOp",EDGE,"E2"),sQuery(id+"F2.wireOp",EDGE,"E3"),sQuery(id+"F2.wireOp",EDGE,"E4"),sQuery(id+"F2.wireOp",EDGE,"E5.filletArc"),sQuery(id+"F2.wireOp",EDGE,"E6.filletArc"),sQuery(id+"F2.wireOp",EDGE,"E7"),sQuery(id+"F2.wireOp",EDGE,"E8"),sQuery(id+"F2.wireOp",EDGE,"E10")])]}),"instanceName":"121"});
            var Q123;
            Q123=makeQuery(id+"F5.opPattern","COPY",BODY,{"derivedFrom":makeQuery(id+"F3.opExtrude","SWEPT_BODY",BODY,{"disambiguationData":[OSD([sQuery(id+"F2.wireOp",EDGE,"E2"),sQuery(id+"F2.wireOp",EDGE,"E3"),sQuery(id+"F2.wireOp",EDGE,"E4"),sQuery(id+"F2.wireOp",EDGE,"E5.filletArc"),sQuery(id+"F2.wireOp",EDGE,"E6.filletArc"),sQuery(id+"F2.wireOp",EDGE,"E7"),sQuery(id+"F2.wireOp",EDGE,"E8"),sQuery(id+"F2.wireOp",EDGE,"E10")])]}),"instanceName":"122"});
            var Q124;
            Q124=makeQuery(id+"F5.opPattern","COPY",BODY,{"derivedFrom":makeQuery(id+"F3.opExtrude","SWEPT_BODY",BODY,{"disambiguationData":[OSD([sQuery(id+"F2.wireOp",EDGE,"E2"),sQuery(id+"F2.wireOp",EDGE,"E3"),sQuery(id+"F2.wireOp",EDGE,"E4"),sQuery(id+"F2.wireOp",EDGE,"E5.filletArc"),sQuery(id+"F2.wireOp",EDGE,"E6.filletArc"),sQuery(id+"F2.wireOp",EDGE,"E7"),sQuery(id+"F2.wireOp",EDGE,"E8"),sQuery(id+"F2.wireOp",EDGE,"E10")])]}),"instanceName":"123"});
            var Q125;
            Q125=makeQuery(id+"F5.opPattern","COPY",BODY,{"derivedFrom":makeQuery(id+"F3.opExtrude","SWEPT_BODY",BODY,{"disambiguationData":[OSD([sQuery(id+"F2.wireOp",EDGE,"E2"),sQuery(id+"F2.wireOp",EDGE,"E3"),sQuery(id+"F2.wireOp",EDGE,"E4"),sQuery(id+"F2.wireOp",EDGE,"E5.filletArc"),sQuery(id+"F2.wireOp",EDGE,"E6.filletArc"),sQuery(id+"F2.wireOp",EDGE,"E7"),sQuery(id+"F2.wireOp",EDGE,"E8"),sQuery(id+"F2.wireOp",EDGE,"E10")])]}),"instanceName":"124"});
            var Q126;
            Q126=makeQuery(id+"F5.opPattern","COPY",BODY,{"derivedFrom":makeQuery(id+"F3.opExtrude","SWEPT_BODY",BODY,{"disambiguationData":[OSD([sQuery(id+"F2.wireOp",EDGE,"E2"),sQuery(id+"F2.wireOp",EDGE,"E3"),sQuery(id+"F2.wireOp",EDGE,"E4"),sQuery(id+"F2.wireOp",EDGE,"E5.filletArc"),sQuery(id+"F2.wireOp",EDGE,"E6.filletArc"),sQuery(id+"F2.wireOp",EDGE,"E7"),sQuery(id+"F2.wireOp",EDGE,"E8"),sQuery(id+"F2.wireOp",EDGE,"E10")])]}),"instanceName":"125"});
            var Q127;
            Q127=makeQuery(id+"F5.opPattern","COPY",BODY,{"derivedFrom":makeQuery(id+"F3.opExtrude","SWEPT_BODY",BODY,{"disambiguationData":[OSD([sQuery(id+"F2.wireOp",EDGE,"E2"),sQuery(id+"F2.wireOp",EDGE,"E3"),sQuery(id+"F2.wireOp",EDGE,"E4"),sQuery(id+"F2.wireOp",EDGE,"E5.filletArc"),sQuery(id+"F2.wireOp",EDGE,"E6.filletArc"),sQuery(id+"F2.wireOp",EDGE,"E7"),sQuery(id+"F2.wireOp",EDGE,"E8"),sQuery(id+"F2.wireOp",EDGE,"E10")])]}),"instanceName":"126"});
            var Q128;
            Q128=makeQuery(id+"F5.opPattern","COPY",BODY,{"derivedFrom":makeQuery(id+"F3.opExtrude","SWEPT_BODY",BODY,{"disambiguationData":[OSD([sQuery(id+"F2.wireOp",EDGE,"E2"),sQuery(id+"F2.wireOp",EDGE,"E3"),sQuery(id+"F2.wireOp",EDGE,"E4"),sQuery(id+"F2.wireOp",EDGE,"E5.filletArc"),sQuery(id+"F2.wireOp",EDGE,"E6.filletArc"),sQuery(id+"F2.wireOp",EDGE,"E7"),sQuery(id+"F2.wireOp",EDGE,"E8"),sQuery(id+"F2.wireOp",EDGE,"E10")])]}),"instanceName":"127"});
            booleanBodies(context, id + "F6", {"operationType" : BooleanOperationType.UNION, "tools" : qUnion([Q0, Q1, Q2, Q3, Q4, Q5, Q6, Q7, Q8, Q9, Q10, Q11, Q12, Q13, Q14, Q15, Q16, Q17, Q18, Q19, Q20, Q21, Q22, Q23, Q24, Q25, Q26, Q27, Q28, Q29, Q30, Q31, Q32, Q33, Q34, Q35, Q36, Q37, Q38, Q39, Q40, Q41, Q42, Q43, Q44, Q45, Q46, Q47, Q48, Q49, Q50, Q51, Q52, Q53, Q54, Q55, Q56, Q57, Q58, Q59, Q60, Q61, Q62, Q63, Q64, Q65, Q66, Q67, Q68, Q69, Q70, Q71, Q72, Q73, Q74, Q75, Q76, Q77, Q78, Q79, Q80, Q81, Q82, Q83, Q84, Q85, Q86, Q87, Q88, Q89, Q90, Q91, Q92, Q93, Q94, Q95, Q96, Q97, Q98, Q99, Q100, Q101, Q102, Q103, Q104, Q105, Q106, Q107, Q108, Q109, Q110, Q111, Q112, Q113, Q114, Q115, Q116, Q117, Q118, Q119, Q120, Q121, Q122, Q123, Q124, Q125, Q126, Q127, Q128])});
        }
        {
            var Q0;
            {var subQ0=sQuery(id+"F0.wireOp",EDGE,"E0");var subQ1=makeQuery(id+"F3.opExtrude","CAP_FACE",FACE,{"disambiguationData":[OSD([subQ0])],"isStart":false});Q0=makeQuery(id+"F6.opBoolean","MERGE",FACE,{"derivedFrom":[makeQuery(id+"F1.opExtrude","CAP_FACE",FACE,{"disambiguationData":[OSD([subQ0])],"isStart":false}),subQ1,makeQuery(id+"F5.opPattern","COPY",FACE,{"derivedFrom":subQ1,"instanceName":"1"}),makeQuery(id+"F5.opPattern","COPY",FACE,{"derivedFrom":subQ1,"instanceName":"2"}),makeQuery(id+"F5.opPattern","COPY",FACE,{"derivedFrom":subQ1,"instanceName":"3"}),makeQuery(id+"F5.opPattern","COPY",FACE,{"derivedFrom":subQ1,"instanceName":"4"}),makeQuery(id+"F5.opPattern","COPY",FACE,{"derivedFrom":subQ1,"instanceName":"5"}),makeQuery(id+"F5.opPattern","COPY",FACE,{"derivedFrom":subQ1,"instanceName":"6"}),makeQuery(id+"F5.opPattern","COPY",FACE,{"derivedFrom":subQ1,"instanceName":"7"}),makeQuery(id+"F5.opPattern","COPY",FACE,{"derivedFrom":subQ1,"instanceName":"8"}),makeQuery(id+"F5.opPattern","COPY",FACE,{"derivedFrom":subQ1,"instanceName":"9"}),makeQuery(id+"F5.opPattern","COPY",FACE,{"derivedFrom":subQ1,"instanceName":"10"}),makeQuery(id+"F5.opPattern","COPY",FACE,{"derivedFrom":subQ1,"instanceName":"11"}),makeQuery(id+"F5.opPattern","COPY",FACE,{"derivedFrom":subQ1,"instanceName":"12"}),makeQuery(id+"F5.opPattern","COPY",FACE,{"derivedFrom":subQ1,"instanceName":"13"}),makeQuery(id+"F5.opPattern","COPY",FACE,{"derivedFrom":subQ1,"instanceName":"14"}),makeQuery(id+"F5.opPattern","COPY",FACE,{"derivedFrom":subQ1,"instanceName":"15"}),makeQuery(id+"F5.opPattern","COPY",FACE,{"derivedFrom":subQ1,"instanceName":"16"}),makeQuery(id+"F5.opPattern","COPY",FACE,{"derivedFrom":subQ1,"instanceName":"17"}),makeQuery(id+"F5.opPattern","COPY",FACE,{"derivedFrom":subQ1,"instanceName":"18"}),makeQuery(id+"F5.opPattern","COPY",FACE,{"derivedFrom":subQ1,"instanceName":"19"}),makeQuery(id+"F5.opPattern","COPY",FACE,{"derivedFrom":subQ1,"instanceName":"20"}),makeQuery(id+"F5.opPattern","COPY",FACE,{"derivedFrom":subQ1,"instanceName":"21"}),makeQuery(id+"F5.opPattern","COPY",FACE,{"derivedFrom":subQ1,"instanceName":"22"}),makeQuery(id+"F5.opPattern","COPY",FACE,{"derivedFrom":subQ1,"instanceName":"23"}),makeQuery(id+"F5.opPattern","COPY",FACE,{"derivedFrom":subQ1,"instanceName":"24"}),makeQuery(id+"F5.opPattern","COPY",FACE,{"derivedFrom":subQ1,"instanceName":"25"}),makeQuery(id+"F5.opPattern","COPY",FACE,{"derivedFrom":subQ1,"instanceName":"26"}),makeQuery(id+"F5.opPattern","COPY",FACE,{"derivedFrom":subQ1,"instanceName":"27"}),makeQuery(id+"F5.opPattern","COPY",FACE,{"derivedFrom":subQ1,"instanceName":"28"}),makeQuery(id+"F5.opPattern","COPY",FACE,{"derivedFrom":subQ1,"instanceName":"29"}),makeQuery(id+"F5.opPattern","COPY",FACE,{"derivedFrom":subQ1,"instanceName":"30"}),makeQuery(id+"F5.opPattern","COPY",FACE,{"derivedFrom":subQ1,"instanceName":"31"}),makeQuery(id+"F5.opPattern","COPY",FACE,{"derivedFrom":subQ1,"instanceName":"32"}),makeQuery(id+"F5.opPattern","COPY",FACE,{"derivedFrom":subQ1,"instanceName":"33"}),makeQuery(id+"F5.opPattern","COPY",FACE,{"derivedFrom":subQ1,"instanceName":"34"}),makeQuery(id+"F5.opPattern","COPY",FACE,{"derivedFrom":subQ1,"instanceName":"35"}),makeQuery(id+"F5.opPattern","COPY",FACE,{"derivedFrom":subQ1,"instanceName":"36"}),makeQuery(id+"F5.opPattern","COPY",FACE,{"derivedFrom":subQ1,"instanceName":"37"}),makeQuery(id+"F5.opPattern","COPY",FACE,{"derivedFrom":subQ1,"instanceName":"38"}),makeQuery(id+"F5.opPattern","COPY",FACE,{"derivedFrom":subQ1,"instanceName":"39"}),makeQuery(id+"F5.opPattern","COPY",FACE,{"derivedFrom":subQ1,"instanceName":"40"}),makeQuery(id+"F5.opPattern","COPY",FACE,{"derivedFrom":subQ1,"instanceName":"41"}),makeQuery(id+"F5.opPattern","COPY",FACE,{"derivedFrom":subQ1,"instanceName":"42"}),makeQuery(id+"F5.opPattern","COPY",FACE,{"derivedFrom":subQ1,"instanceName":"43"}),makeQuery(id+"F5.opPattern","COPY",FACE,{"derivedFrom":subQ1,"instanceName":"44"}),makeQuery(id+"F5.opPattern","COPY",FACE,{"derivedFrom":subQ1,"instanceName":"45"}),makeQuery(id+"F5.opPattern","COPY",FACE,{"derivedFrom":subQ1,"instanceName":"46"}),makeQuery(id+"F5.opPattern","COPY",FACE,{"derivedFrom":subQ1,"instanceName":"47"}),makeQuery(id+"F5.opPattern","COPY",FACE,{"derivedFrom":subQ1,"instanceName":"48"}),makeQuery(id+"F5.opPattern","COPY",FACE,{"derivedFrom":subQ1,"instanceName":"49"}),makeQuery(id+"F5.opPattern","COPY",FACE,{"derivedFrom":subQ1,"instanceName":"50"}),makeQuery(id+"F5.opPattern","COPY",FACE,{"derivedFrom":subQ1,"instanceName":"51"}),makeQuery(id+"F5.opPattern","COPY",FACE,{"derivedFrom":subQ1,"instanceName":"52"}),makeQuery(id+"F5.opPattern","COPY",FACE,{"derivedFrom":subQ1,"instanceName":"53"}),makeQuery(id+"F5.opPattern","COPY",FACE,{"derivedFrom":subQ1,"instanceName":"54"}),makeQuery(id+"F5.opPattern","COPY",FACE,{"derivedFrom":subQ1,"instanceName":"55"}),makeQuery(id+"F5.opPattern","COPY",FACE,{"derivedFrom":subQ1,"instanceName":"56"}),makeQuery(id+"F5.opPattern","COPY",FACE,{"derivedFrom":subQ1,"instanceName":"57"}),makeQuery(id+"F5.opPattern","COPY",FACE,{"derivedFrom":subQ1,"instanceName":"58"}),makeQuery(id+"F5.opPattern","COPY",FACE,{"derivedFrom":subQ1,"instanceName":"59"}),makeQuery(id+"F5.opPattern","COPY",FACE,{"derivedFrom":subQ1,"instanceName":"60"}),makeQuery(id+"F5.opPattern","COPY",FACE,{"derivedFrom":subQ1,"instanceName":"61"}),makeQuery(id+"F5.opPattern","COPY",FACE,{"derivedFrom":subQ1,"instanceName":"62"}),makeQuery(id+"F5.opPattern","COPY",FACE,{"derivedFrom":subQ1,"instanceName":"63"}),makeQuery(id+"F5.opPattern","COPY",FACE,{"derivedFrom":subQ1,"instanceName":"64"}),makeQuery(id+"F5.opPattern","COPY",FACE,{"derivedFrom":subQ1,"instanceName":"65"}),makeQuery(id+"F5.opPattern","COPY",FACE,{"derivedFrom":subQ1,"instanceName":"66"}),makeQuery(id+"F5.opPattern","COPY",FACE,{"derivedFrom":subQ1,"instanceName":"67"}),makeQuery(id+"F5.opPattern","COPY",FACE,{"derivedFrom":subQ1,"instanceName":"68"}),makeQuery(id+"F5.opPattern","COPY",FACE,{"derivedFrom":subQ1,"instanceName":"69"}),makeQuery(id+"F5.opPattern","COPY",FACE,{"derivedFrom":subQ1,"instanceName":"70"}),makeQuery(id+"F5.opPattern","COPY",FACE,{"derivedFrom":subQ1,"instanceName":"71"}),makeQuery(id+"F5.opPattern","COPY",FACE,{"derivedFrom":subQ1,"instanceName":"72"}),makeQuery(id+"F5.opPattern","COPY",FACE,{"derivedFrom":subQ1,"instanceName":"73"}),makeQuery(id+"F5.opPattern","COPY",FACE,{"derivedFrom":subQ1,"instanceName":"74"}),makeQuery(id+"F5.opPattern","COPY",FACE,{"derivedFrom":subQ1,"instanceName":"75"}),makeQuery(id+"F5.opPattern","COPY",FACE,{"derivedFrom":subQ1,"instanceName":"76"}),makeQuery(id+"F5.opPattern","COPY",FACE,{"derivedFrom":subQ1,"instanceName":"77"}),makeQuery(id+"F5.opPattern","COPY",FACE,{"derivedFrom":subQ1,"instanceName":"78"}),makeQuery(id+"F5.opPattern","COPY",FACE,{"derivedFrom":subQ1,"instanceName":"79"}),makeQuery(id+"F5.opPattern","COPY",FACE,{"derivedFrom":subQ1,"instanceName":"80"}),makeQuery(id+"F5.opPattern","COPY",FACE,{"derivedFrom":subQ1,"instanceName":"81"}),makeQuery(id+"F5.opPattern","COPY",FACE,{"derivedFrom":subQ1,"instanceName":"82"}),makeQuery(id+"F5.opPattern","COPY",FACE,{"derivedFrom":subQ1,"instanceName":"83"}),makeQuery(id+"F5.opPattern","COPY",FACE,{"derivedFrom":subQ1,"instanceName":"84"}),makeQuery(id+"F5.opPattern","COPY",FACE,{"derivedFrom":subQ1,"instanceName":"85"}),makeQuery(id+"F5.opPattern","COPY",FACE,{"derivedFrom":subQ1,"instanceName":"86"}),makeQuery(id+"F5.opPattern","COPY",FACE,{"derivedFrom":subQ1,"instanceName":"87"}),makeQuery(id+"F5.opPattern","COPY",FACE,{"derivedFrom":subQ1,"instanceName":"88"}),makeQuery(id+"F5.opPattern","COPY",FACE,{"derivedFrom":subQ1,"instanceName":"89"}),makeQuery(id+"F5.opPattern","COPY",FACE,{"derivedFrom":subQ1,"instanceName":"90"}),makeQuery(id+"F5.opPattern","COPY",FACE,{"derivedFrom":subQ1,"instanceName":"91"}),makeQuery(id+"F5.opPattern","COPY",FACE,{"derivedFrom":subQ1,"instanceName":"92"}),makeQuery(id+"F5.opPattern","COPY",FACE,{"derivedFrom":subQ1,"instanceName":"93"}),makeQuery(id+"F5.opPattern","COPY",FACE,{"derivedFrom":subQ1,"instanceName":"94"}),makeQuery(id+"F5.opPattern","COPY",FACE,{"derivedFrom":subQ1,"instanceName":"95"}),makeQuery(id+"F5.opPattern","COPY",FACE,{"derivedFrom":subQ1,"instanceName":"96"}),makeQuery(id+"F5.opPattern","COPY",FACE,{"derivedFrom":subQ1,"instanceName":"97"}),makeQuery(id+"F5.opPattern","COPY",FACE,{"derivedFrom":subQ1,"instanceName":"98"}),makeQuery(id+"F5.opPattern","COPY",FACE,{"derivedFrom":subQ1,"instanceName":"99"}),makeQuery(id+"F5.opPattern","COPY",FACE,{"derivedFrom":subQ1,"instanceName":"100"}),makeQuery(id+"F5.opPattern","COPY",FACE,{"derivedFrom":subQ1,"instanceName":"101"}),makeQuery(id+"F5.opPattern","COPY",FACE,{"derivedFrom":subQ1,"instanceName":"102"}),makeQuery(id+"F5.opPattern","COPY",FACE,{"derivedFrom":subQ1,"instanceName":"103"}),makeQuery(id+"F5.opPattern","COPY",FACE,{"derivedFrom":subQ1,"instanceName":"104"}),makeQuery(id+"F5.opPattern","COPY",FACE,{"derivedFrom":subQ1,"instanceName":"105"}),makeQuery(id+"F5.opPattern","COPY",FACE,{"derivedFrom":subQ1,"instanceName":"106"}),makeQuery(id+"F5.opPattern","COPY",FACE,{"derivedFrom":subQ1,"instanceName":"107"}),makeQuery(id+"F5.opPattern","COPY",FACE,{"derivedFrom":subQ1,"instanceName":"108"}),makeQuery(id+"F5.opPattern","COPY",FACE,{"derivedFrom":subQ1,"instanceName":"109"}),makeQuery(id+"F5.opPattern","COPY",FACE,{"derivedFrom":subQ1,"instanceName":"110"}),makeQuery(id+"F5.opPattern","COPY",FACE,{"derivedFrom":subQ1,"instanceName":"111"}),makeQuery(id+"F5.opPattern","COPY",FACE,{"derivedFrom":subQ1,"instanceName":"112"}),makeQuery(id+"F5.opPattern","COPY",FACE,{"derivedFrom":subQ1,"instanceName":"113"}),makeQuery(id+"F5.opPattern","COPY",FACE,{"derivedFrom":subQ1,"instanceName":"114"}),makeQuery(id+"F5.opPattern","COPY",FACE,{"derivedFrom":subQ1,"instanceName":"115"}),makeQuery(id+"F5.opPattern","COPY",FACE,{"derivedFrom":subQ1,"instanceName":"116"}),makeQuery(id+"F5.opPattern","COPY",FACE,{"derivedFrom":subQ1,"instanceName":"117"}),makeQuery(id+"F5.opPattern","COPY",FACE,{"derivedFrom":subQ1,"instanceName":"118"}),makeQuery(id+"F5.opPattern","COPY",FACE,{"derivedFrom":subQ1,"instanceName":"119"}),makeQuery(id+"F5.opPattern","COPY",FACE,{"derivedFrom":subQ1,"instanceName":"120"}),makeQuery(id+"F5.opPattern","COPY",FACE,{"derivedFrom":subQ1,"instanceName":"121"}),makeQuery(id+"F5.opPattern","COPY",FACE,{"derivedFrom":subQ1,"instanceName":"122"}),makeQuery(id+"F5.opPattern","COPY",FACE,{"derivedFrom":subQ1,"instanceName":"123"}),makeQuery(id+"F5.opPattern","COPY",FACE,{"derivedFrom":subQ1,"instanceName":"124"}),makeQuery(id+"F5.opPattern","COPY",FACE,{"derivedFrom":subQ1,"instanceName":"125"}),makeQuery(id+"F5.opPattern","COPY",FACE,{"derivedFrom":subQ1,"instanceName":"126"}),makeQuery(id+"F5.opPattern","COPY",FACE,{"derivedFrom":subQ1,"instanceName":"127"})]});}
            var sketch = newSketch(context, id + "F7", { "sketchPlane" : qUnion([Q0])});
            skCircle(sketch, "E12", {"center": v(0, 0) * mm, "radius": 30.23 * mm});
            skSolve(sketch);
        }
        {
            var Q0;
            Q0=qSketchRegion(id+"F7",true);
            extrude(context, id + "F8", {"entities" : qUnion([Q0]), "operationType" : NewBodyOperationType.REMOVE, "oppositeDirection" : true, "depth" : 25.4 * mm});
        }
        {
            var Q0;
            {var subQ0=sQuery(id+"F0.wireOp",EDGE,"E0");var subQ1=makeQuery(id+"F3.opExtrude","CAP_FACE",FACE,{"disambiguationData":[OSD([subQ0])],"isStart":false});Q0=makeQuery(id+"F6.opBoolean","MERGE",FACE,{"derivedFrom":[makeQuery(id+"F1.opExtrude","CAP_FACE",FACE,{"disambiguationData":[OSD([subQ0])],"isStart":false}),subQ1,makeQuery(id+"F5.opPattern","COPY",FACE,{"derivedFrom":subQ1,"instanceName":"1"}),makeQuery(id+"F5.opPattern","COPY",FACE,{"derivedFrom":subQ1,"instanceName":"2"}),makeQuery(id+"F5.opPattern","COPY",FACE,{"derivedFrom":subQ1,"instanceName":"3"}),makeQuery(id+"F5.opPattern","COPY",FACE,{"derivedFrom":subQ1,"instanceName":"4"}),makeQuery(id+"F5.opPattern","COPY",FACE,{"derivedFrom":subQ1,"instanceName":"5"}),makeQuery(id+"F5.opPattern","COPY",FACE,{"derivedFrom":subQ1,"instanceName":"6"}),makeQuery(id+"F5.opPattern","COPY",FACE,{"derivedFrom":subQ1,"instanceName":"7"}),makeQuery(id+"F5.opPattern","COPY",FACE,{"derivedFrom":subQ1,"instanceName":"8"}),makeQuery(id+"F5.opPattern","COPY",FACE,{"derivedFrom":subQ1,"instanceName":"9"}),makeQuery(id+"F5.opPattern","COPY",FACE,{"derivedFrom":subQ1,"instanceName":"10"}),makeQuery(id+"F5.opPattern","COPY",FACE,{"derivedFrom":subQ1,"instanceName":"11"}),makeQuery(id+"F5.opPattern","COPY",FACE,{"derivedFrom":subQ1,"instanceName":"12"}),makeQuery(id+"F5.opPattern","COPY",FACE,{"derivedFrom":subQ1,"instanceName":"13"}),makeQuery(id+"F5.opPattern","COPY",FACE,{"derivedFrom":subQ1,"instanceName":"14"}),makeQuery(id+"F5.opPattern","COPY",FACE,{"derivedFrom":subQ1,"instanceName":"15"}),makeQuery(id+"F5.opPattern","COPY",FACE,{"derivedFrom":subQ1,"instanceName":"16"}),makeQuery(id+"F5.opPattern","COPY",FACE,{"derivedFrom":subQ1,"instanceName":"17"}),makeQuery(id+"F5.opPattern","COPY",FACE,{"derivedFrom":subQ1,"instanceName":"18"}),makeQuery(id+"F5.opPattern","COPY",FACE,{"derivedFrom":subQ1,"instanceName":"19"}),makeQuery(id+"F5.opPattern","COPY",FACE,{"derivedFrom":subQ1,"instanceName":"20"}),makeQuery(id+"F5.opPattern","COPY",FACE,{"derivedFrom":subQ1,"instanceName":"21"}),makeQuery(id+"F5.opPattern","COPY",FACE,{"derivedFrom":subQ1,"instanceName":"22"}),makeQuery(id+"F5.opPattern","COPY",FACE,{"derivedFrom":subQ1,"instanceName":"23"}),makeQuery(id+"F5.opPattern","COPY",FACE,{"derivedFrom":subQ1,"instanceName":"24"}),makeQuery(id+"F5.opPattern","COPY",FACE,{"derivedFrom":subQ1,"instanceName":"25"}),makeQuery(id+"F5.opPattern","COPY",FACE,{"derivedFrom":subQ1,"instanceName":"26"}),makeQuery(id+"F5.opPattern","COPY",FACE,{"derivedFrom":subQ1,"instanceName":"27"}),makeQuery(id+"F5.opPattern","COPY",FACE,{"derivedFrom":subQ1,"instanceName":"28"}),makeQuery(id+"F5.opPattern","COPY",FACE,{"derivedFrom":subQ1,"instanceName":"29"}),makeQuery(id+"F5.opPattern","COPY",FACE,{"derivedFrom":subQ1,"instanceName":"30"}),makeQuery(id+"F5.opPattern","COPY",FACE,{"derivedFrom":subQ1,"instanceName":"31"}),makeQuery(id+"F5.opPattern","COPY",FACE,{"derivedFrom":subQ1,"instanceName":"32"}),makeQuery(id+"F5.opPattern","COPY",FACE,{"derivedFrom":subQ1,"instanceName":"33"}),makeQuery(id+"F5.opPattern","COPY",FACE,{"derivedFrom":subQ1,"instanceName":"34"}),makeQuery(id+"F5.opPattern","COPY",FACE,{"derivedFrom":subQ1,"instanceName":"35"}),makeQuery(id+"F5.opPattern","COPY",FACE,{"derivedFrom":subQ1,"instanceName":"36"}),makeQuery(id+"F5.opPattern","COPY",FACE,{"derivedFrom":subQ1,"instanceName":"37"}),makeQuery(id+"F5.opPattern","COPY",FACE,{"derivedFrom":subQ1,"instanceName":"38"}),makeQuery(id+"F5.opPattern","COPY",FACE,{"derivedFrom":subQ1,"instanceName":"39"}),makeQuery(id+"F5.opPattern","COPY",FACE,{"derivedFrom":subQ1,"instanceName":"40"}),makeQuery(id+"F5.opPattern","COPY",FACE,{"derivedFrom":subQ1,"instanceName":"41"}),makeQuery(id+"F5.opPattern","COPY",FACE,{"derivedFrom":subQ1,"instanceName":"42"}),makeQuery(id+"F5.opPattern","COPY",FACE,{"derivedFrom":subQ1,"instanceName":"43"}),makeQuery(id+"F5.opPattern","COPY",FACE,{"derivedFrom":subQ1,"instanceName":"44"}),makeQuery(id+"F5.opPattern","COPY",FACE,{"derivedFrom":subQ1,"instanceName":"45"}),makeQuery(id+"F5.opPattern","COPY",FACE,{"derivedFrom":subQ1,"instanceName":"46"}),makeQuery(id+"F5.opPattern","COPY",FACE,{"derivedFrom":subQ1,"instanceName":"47"}),makeQuery(id+"F5.opPattern","COPY",FACE,{"derivedFrom":subQ1,"instanceName":"48"}),makeQuery(id+"F5.opPattern","COPY",FACE,{"derivedFrom":subQ1,"instanceName":"49"}),makeQuery(id+"F5.opPattern","COPY",FACE,{"derivedFrom":subQ1,"instanceName":"50"}),makeQuery(id+"F5.opPattern","COPY",FACE,{"derivedFrom":subQ1,"instanceName":"51"}),makeQuery(id+"F5.opPattern","COPY",FACE,{"derivedFrom":subQ1,"instanceName":"52"}),makeQuery(id+"F5.opPattern","COPY",FACE,{"derivedFrom":subQ1,"instanceName":"53"}),makeQuery(id+"F5.opPattern","COPY",FACE,{"derivedFrom":subQ1,"instanceName":"54"}),makeQuery(id+"F5.opPattern","COPY",FACE,{"derivedFrom":subQ1,"instanceName":"55"}),makeQuery(id+"F5.opPattern","COPY",FACE,{"derivedFrom":subQ1,"instanceName":"56"}),makeQuery(id+"F5.opPattern","COPY",FACE,{"derivedFrom":subQ1,"instanceName":"57"}),makeQuery(id+"F5.opPattern","COPY",FACE,{"derivedFrom":subQ1,"instanceName":"58"}),makeQuery(id+"F5.opPattern","COPY",FACE,{"derivedFrom":subQ1,"instanceName":"59"}),makeQuery(id+"F5.opPattern","COPY",FACE,{"derivedFrom":subQ1,"instanceName":"60"}),makeQuery(id+"F5.opPattern","COPY",FACE,{"derivedFrom":subQ1,"instanceName":"61"}),makeQuery(id+"F5.opPattern","COPY",FACE,{"derivedFrom":subQ1,"instanceName":"62"}),makeQuery(id+"F5.opPattern","COPY",FACE,{"derivedFrom":subQ1,"instanceName":"63"}),makeQuery(id+"F5.opPattern","COPY",FACE,{"derivedFrom":subQ1,"instanceName":"64"}),makeQuery(id+"F5.opPattern","COPY",FACE,{"derivedFrom":subQ1,"instanceName":"65"}),makeQuery(id+"F5.opPattern","COPY",FACE,{"derivedFrom":subQ1,"instanceName":"66"}),makeQuery(id+"F5.opPattern","COPY",FACE,{"derivedFrom":subQ1,"instanceName":"67"}),makeQuery(id+"F5.opPattern","COPY",FACE,{"derivedFrom":subQ1,"instanceName":"68"}),makeQuery(id+"F5.opPattern","COPY",FACE,{"derivedFrom":subQ1,"instanceName":"69"}),makeQuery(id+"F5.opPattern","COPY",FACE,{"derivedFrom":subQ1,"instanceName":"70"}),makeQuery(id+"F5.opPattern","COPY",FACE,{"derivedFrom":subQ1,"instanceName":"71"}),makeQuery(id+"F5.opPattern","COPY",FACE,{"derivedFrom":subQ1,"instanceName":"72"}),makeQuery(id+"F5.opPattern","COPY",FACE,{"derivedFrom":subQ1,"instanceName":"73"}),makeQuery(id+"F5.opPattern","COPY",FACE,{"derivedFrom":subQ1,"instanceName":"74"}),makeQuery(id+"F5.opPattern","COPY",FACE,{"derivedFrom":subQ1,"instanceName":"75"}),makeQuery(id+"F5.opPattern","COPY",FACE,{"derivedFrom":subQ1,"instanceName":"76"}),makeQuery(id+"F5.opPattern","COPY",FACE,{"derivedFrom":subQ1,"instanceName":"77"}),makeQuery(id+"F5.opPattern","COPY",FACE,{"derivedFrom":subQ1,"instanceName":"78"}),makeQuery(id+"F5.opPattern","COPY",FACE,{"derivedFrom":subQ1,"instanceName":"79"}),makeQuery(id+"F5.opPattern","COPY",FACE,{"derivedFrom":subQ1,"instanceName":"80"}),makeQuery(id+"F5.opPattern","COPY",FACE,{"derivedFrom":subQ1,"instanceName":"81"}),makeQuery(id+"F5.opPattern","COPY",FACE,{"derivedFrom":subQ1,"instanceName":"82"}),makeQuery(id+"F5.opPattern","COPY",FACE,{"derivedFrom":subQ1,"instanceName":"83"}),makeQuery(id+"F5.opPattern","COPY",FACE,{"derivedFrom":subQ1,"instanceName":"84"}),makeQuery(id+"F5.opPattern","COPY",FACE,{"derivedFrom":subQ1,"instanceName":"85"}),makeQuery(id+"F5.opPattern","COPY",FACE,{"derivedFrom":subQ1,"instanceName":"86"}),makeQuery(id+"F5.opPattern","COPY",FACE,{"derivedFrom":subQ1,"instanceName":"87"}),makeQuery(id+"F5.opPattern","COPY",FACE,{"derivedFrom":subQ1,"instanceName":"88"}),makeQuery(id+"F5.opPattern","COPY",FACE,{"derivedFrom":subQ1,"instanceName":"89"}),makeQuery(id+"F5.opPattern","COPY",FACE,{"derivedFrom":subQ1,"instanceName":"90"}),makeQuery(id+"F5.opPattern","COPY",FACE,{"derivedFrom":subQ1,"instanceName":"91"}),makeQuery(id+"F5.opPattern","COPY",FACE,{"derivedFrom":subQ1,"instanceName":"92"}),makeQuery(id+"F5.opPattern","COPY",FACE,{"derivedFrom":subQ1,"instanceName":"93"}),makeQuery(id+"F5.opPattern","COPY",FACE,{"derivedFrom":subQ1,"instanceName":"94"}),makeQuery(id+"F5.opPattern","COPY",FACE,{"derivedFrom":subQ1,"instanceName":"95"}),makeQuery(id+"F5.opPattern","COPY",FACE,{"derivedFrom":subQ1,"instanceName":"96"}),makeQuery(id+"F5.opPattern","COPY",FACE,{"derivedFrom":subQ1,"instanceName":"97"}),makeQuery(id+"F5.opPattern","COPY",FACE,{"derivedFrom":subQ1,"instanceName":"98"}),makeQuery(id+"F5.opPattern","COPY",FACE,{"derivedFrom":subQ1,"instanceName":"99"}),makeQuery(id+"F5.opPattern","COPY",FACE,{"derivedFrom":subQ1,"instanceName":"100"}),makeQuery(id+"F5.opPattern","COPY",FACE,{"derivedFrom":subQ1,"instanceName":"101"}),makeQuery(id+"F5.opPattern","COPY",FACE,{"derivedFrom":subQ1,"instanceName":"102"}),makeQuery(id+"F5.opPattern","COPY",FACE,{"derivedFrom":subQ1,"instanceName":"103"}),makeQuery(id+"F5.opPattern","COPY",FACE,{"derivedFrom":subQ1,"instanceName":"104"}),makeQuery(id+"F5.opPattern","COPY",FACE,{"derivedFrom":subQ1,"instanceName":"105"}),makeQuery(id+"F5.opPattern","COPY",FACE,{"derivedFrom":subQ1,"instanceName":"106"}),makeQuery(id+"F5.opPattern","COPY",FACE,{"derivedFrom":subQ1,"instanceName":"107"}),makeQuery(id+"F5.opPattern","COPY",FACE,{"derivedFrom":subQ1,"instanceName":"108"}),makeQuery(id+"F5.opPattern","COPY",FACE,{"derivedFrom":subQ1,"instanceName":"109"}),makeQuery(id+"F5.opPattern","COPY",FACE,{"derivedFrom":subQ1,"instanceName":"110"}),makeQuery(id+"F5.opPattern","COPY",FACE,{"derivedFrom":subQ1,"instanceName":"111"}),makeQuery(id+"F5.opPattern","COPY",FACE,{"derivedFrom":subQ1,"instanceName":"112"}),makeQuery(id+"F5.opPattern","COPY",FACE,{"derivedFrom":subQ1,"instanceName":"113"}),makeQuery(id+"F5.opPattern","COPY",FACE,{"derivedFrom":subQ1,"instanceName":"114"}),makeQuery(id+"F5.opPattern","COPY",FACE,{"derivedFrom":subQ1,"instanceName":"115"}),makeQuery(id+"F5.opPattern","COPY",FACE,{"derivedFrom":subQ1,"instanceName":"116"}),makeQuery(id+"F5.opPattern","COPY",FACE,{"derivedFrom":subQ1,"instanceName":"117"}),makeQuery(id+"F5.opPattern","COPY",FACE,{"derivedFrom":subQ1,"instanceName":"118"}),makeQuery(id+"F5.opPattern","COPY",FACE,{"derivedFrom":subQ1,"instanceName":"119"}),makeQuery(id+"F5.opPattern","COPY",FACE,{"derivedFrom":subQ1,"instanceName":"120"}),makeQuery(id+"F5.opPattern","COPY",FACE,{"derivedFrom":subQ1,"instanceName":"121"}),makeQuery(id+"F5.opPattern","COPY",FACE,{"derivedFrom":subQ1,"instanceName":"122"}),makeQuery(id+"F5.opPattern","COPY",FACE,{"derivedFrom":subQ1,"instanceName":"123"}),makeQuery(id+"F5.opPattern","COPY",FACE,{"derivedFrom":subQ1,"instanceName":"124"}),makeQuery(id+"F5.opPattern","COPY",FACE,{"derivedFrom":subQ1,"instanceName":"125"}),makeQuery(id+"F5.opPattern","COPY",FACE,{"derivedFrom":subQ1,"instanceName":"126"}),makeQuery(id+"F5.opPattern","COPY",FACE,{"derivedFrom":subQ1,"instanceName":"127"})]});}
            var sketch = newSketch(context, id + "F9", { "sketchPlane" : qUnion([Q0])});
            skCircle(sketch, "E13", {"center": v(0, 0) * mm, "radius": 155.58 * mm});
            skSolve(sketch);
        }
    });
